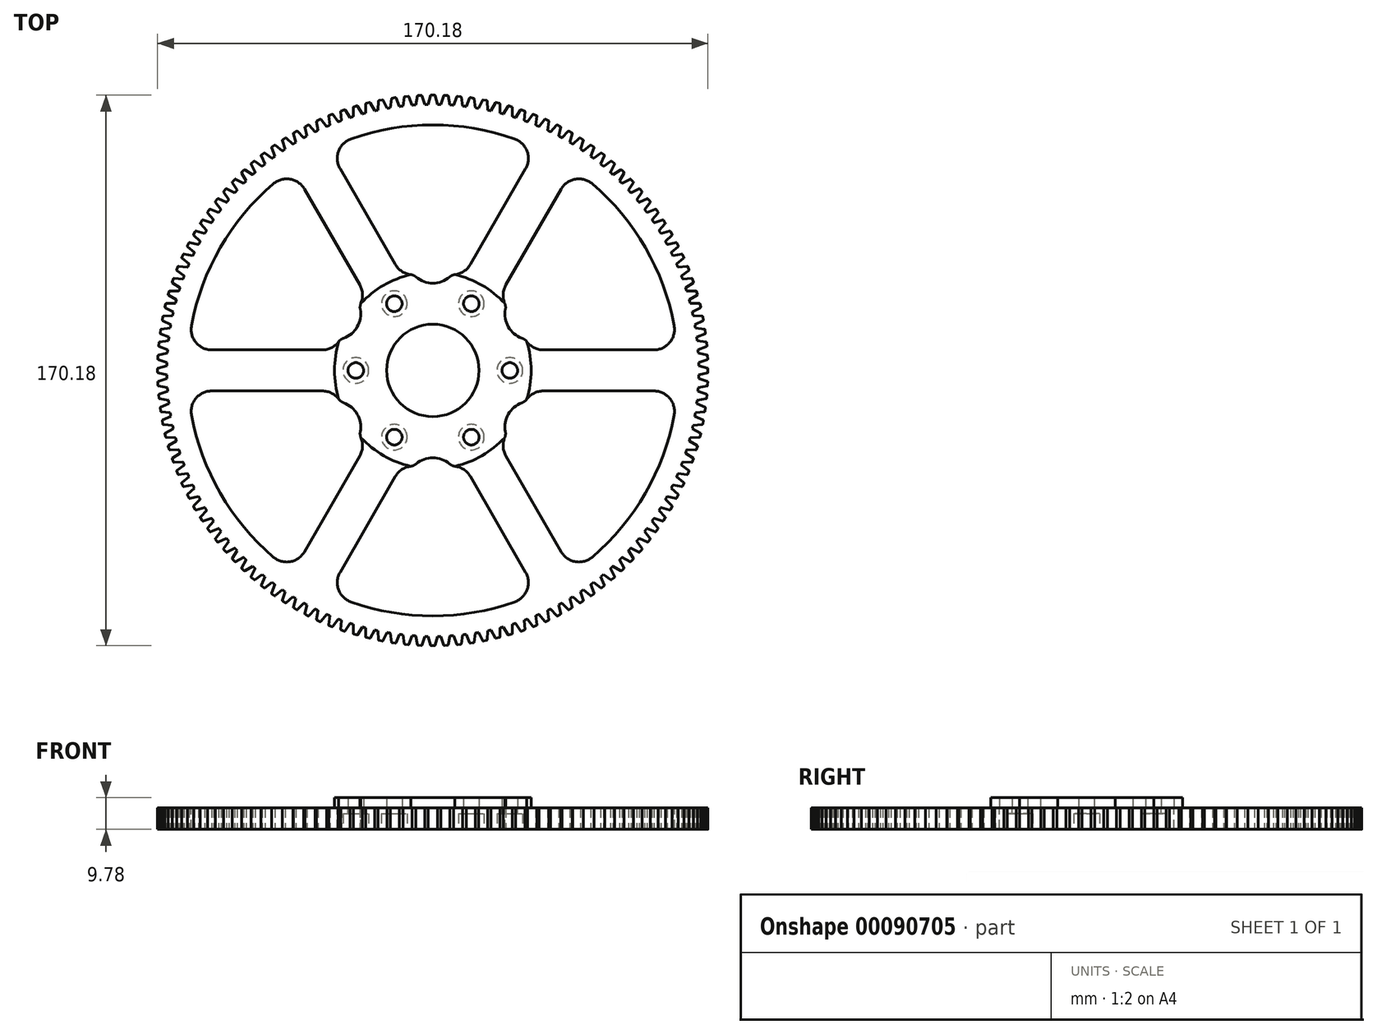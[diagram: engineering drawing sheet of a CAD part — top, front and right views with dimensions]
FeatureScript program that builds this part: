
annotation { "Feature Type Name" : "Feature", "Feature Type Description" : "" }
export const myFeature = defineFeature(function(context is Context, id is Id, definition is map)
    precondition{}
    {
        {
            var Q0;
            Q0=qCreatedBy(makeId("Top.planeOp"),FACE);
            var sketch = newSketch(context, id + "F0", { "sketchPlane" : qUnion([Q0])});
            skArc(sketch, "E0", {"start": v(-1.4, 82.23) * mm, "mid": v(-82.23, -1.4) * mm, "end": v(1.4, -82.23) * mm});
            skArc(sketch, "E1", {"start": v(1.4, -82.23) * mm, "mid": v(82.24, 0) * mm, "end": v(1.4, 82.23) * mm});
            skLineSegment(sketch, "E2", {"start": v(1.4, 82.23) * mm, "end": v(0.7, 84.97) * mm});
            skArc(sketch, "E3", {"start": v(0.7, 84.97) * mm, "mid": v(0.64, 85.06) * mm, "end": v(0.55, 85.1) * mm});
            skLineSegment(sketch, "E4", {"start": v(-1.4, 82.23) * mm, "end": v(-0.7, 84.97) * mm});
            skArc(sketch, "E5", {"start": v(-0.55, 85.1) * mm, "mid": v(-0.64, 85.06) * mm, "end": v(-0.7, 84.97) * mm});
            skLineSegment(sketch, "E6", {"start": v(-0.55, 85.1) * mm, "end": v(0.55, 85.1) * mm});
            skArc(sketch, "E7", {"start": v(1.4, 82.23) * mm, "mid": v(0, 82.24) * mm, "end": v(-1.4, 82.23) * mm});
            skSolve(sketch);
        }
        {
            var Q0;
            Q0=makeQuery(id+"F0.imprint","IMPRINT",FACE,{"disambiguationData":[TD([[makeQuery(id+"F0.imprint","IMPRINT",EDGE,{"derivedFrom":sQuery(id+"F0.wireOp",EDGE,"E0")}),1.0]])]});
            extrude(context, id + "F1", {"entities" : qUnion([Q0]), "endBound" : BoundingType.SYMMETRIC, "depth" : 6.6 * mm});
        }
        {
            var Q0;
            Q0=makeQuery(id+"F0.imprint","IMPRINT",FACE,{"disambiguationData":[TD([[makeQuery(id+"F0.imprint","IMPRINT",EDGE,{"derivedFrom":sQuery(id+"F0.wireOp",EDGE,"E2")}),1.0]])]});
            var Q1;
            Q1=makeQuery(id+"F1.opExtrude","CAP_FACE",FACE,{"disambiguationData":[OSD([sQuery(id+"F0.wireOp",EDGE,"E0"),sQuery(id+"F0.wireOp",EDGE,"E1"),sQuery(id+"F0.wireOp",EDGE,"E7")])],"isStart":false});
            var Q2;
            Q2=makeQuery(id+"F1.opExtrude","CAP_FACE",FACE,{"disambiguationData":[OSD([sQuery(id+"F0.wireOp",EDGE,"E0"),sQuery(id+"F0.wireOp",EDGE,"E1"),sQuery(id+"F0.wireOp",EDGE,"E7")])],"isStart":true});
            extrude(context, id + "F2", {"entities" : qUnion([Q0]), "endBound" : BoundingType.UP_TO_SURFACE, "endBoundEntityFace" : qUnion([Q1]), "depth" : 25.4 * mm, "hasSecondDirection" : true, "secondDirectionBound" : SecondDirectionBoundingType.UP_TO_SURFACE, "secondDirectionOppositeDirection" : true, "secondDirectionBoundEntityFace" : qUnion([Q2]), "secondDirectionDepth" : 25.4 * mm});
        }
        {
            var Q0;
            Q0=makeQuery(id+"F2.opExtrude","SWEPT_BODY",BODY,{"disambiguationData":[OSD([sQuery(id+"F0.wireOp",EDGE,"E2"),sQuery(id+"F0.wireOp",EDGE,"E3"),sQuery(id+"F0.wireOp",EDGE,"E4"),sQuery(id+"F0.wireOp",EDGE,"E5"),sQuery(id+"F0.wireOp",EDGE,"E6"),sQuery(id+"F0.wireOp",EDGE,"E7")])]});
            var Q1;
            Q1=makeQuery(id+"F1.opExtrude","CAP_EDGE",EDGE,{"disambiguationData":[OSD([sQuery(id+"F0.wireOp",EDGE,"E0"),sQuery(id+"F0.wireOp",EDGE,"E1"),sQuery(id+"F0.wireOp",EDGE,"E7")])],"isStart":false});
            circularPattern(context, id + "F3", {"operationType" : NewBodyOperationType.ADD, "entities" : qUnion([Q0]), "axis" : qUnion([Q1]), "angle" : 360 * degree, "instanceCount" : 132, "oppositeDirection" : true, "equalSpace" : true});
        }
        {
            var Q0;
            {var subQ0=sQuery(id+"F0.wireOp",EDGE,"E7");var subQ1=makeQuery(id+"F2.opExtrude","CAP_FACE",FACE,{"disambiguationData":[OSD([sQuery(id+"F0.wireOp",EDGE,"E2"),sQuery(id+"F0.wireOp",EDGE,"E3"),sQuery(id+"F0.wireOp",EDGE,"E4"),sQuery(id+"F0.wireOp",EDGE,"E5"),sQuery(id+"F0.wireOp",EDGE,"E6"),subQ0])],"isStart":false});Q0=makeQuery(id+"F3.boolean.opBoolean","MERGE",FACE,{"derivedFrom":[makeQuery(id+"F1.opExtrude","CAP_FACE",FACE,{"disambiguationData":[OSD([sQuery(id+"F0.wireOp",EDGE,"E0"),sQuery(id+"F0.wireOp",EDGE,"E1"),subQ0])],"isStart":false}),subQ1,makeQuery(id+"F3.opPattern","COPY",FACE,{"derivedFrom":subQ1,"instanceName":"1"}),makeQuery(id+"F3.opPattern","COPY",FACE,{"derivedFrom":subQ1,"instanceName":"2"}),makeQuery(id+"F3.opPattern","COPY",FACE,{"derivedFrom":subQ1,"instanceName":"3"}),makeQuery(id+"F3.opPattern","COPY",FACE,{"derivedFrom":subQ1,"instanceName":"4"}),makeQuery(id+"F3.opPattern","COPY",FACE,{"derivedFrom":subQ1,"instanceName":"5"}),makeQuery(id+"F3.opPattern","COPY",FACE,{"derivedFrom":subQ1,"instanceName":"6"}),makeQuery(id+"F3.opPattern","COPY",FACE,{"derivedFrom":subQ1,"instanceName":"7"}),makeQuery(id+"F3.opPattern","COPY",FACE,{"derivedFrom":subQ1,"instanceName":"8"}),makeQuery(id+"F3.opPattern","COPY",FACE,{"derivedFrom":subQ1,"instanceName":"9"}),makeQuery(id+"F3.opPattern","COPY",FACE,{"derivedFrom":subQ1,"instanceName":"10"}),makeQuery(id+"F3.opPattern","COPY",FACE,{"derivedFrom":subQ1,"instanceName":"11"}),makeQuery(id+"F3.opPattern","COPY",FACE,{"derivedFrom":subQ1,"instanceName":"12"}),makeQuery(id+"F3.opPattern","COPY",FACE,{"derivedFrom":subQ1,"instanceName":"13"}),makeQuery(id+"F3.opPattern","COPY",FACE,{"derivedFrom":subQ1,"instanceName":"14"}),makeQuery(id+"F3.opPattern","COPY",FACE,{"derivedFrom":subQ1,"instanceName":"15"}),makeQuery(id+"F3.opPattern","COPY",FACE,{"derivedFrom":subQ1,"instanceName":"16"}),makeQuery(id+"F3.opPattern","COPY",FACE,{"derivedFrom":subQ1,"instanceName":"17"}),makeQuery(id+"F3.opPattern","COPY",FACE,{"derivedFrom":subQ1,"instanceName":"18"}),makeQuery(id+"F3.opPattern","COPY",FACE,{"derivedFrom":subQ1,"instanceName":"19"}),makeQuery(id+"F3.opPattern","COPY",FACE,{"derivedFrom":subQ1,"instanceName":"20"}),makeQuery(id+"F3.opPattern","COPY",FACE,{"derivedFrom":subQ1,"instanceName":"21"}),makeQuery(id+"F3.opPattern","COPY",FACE,{"derivedFrom":subQ1,"instanceName":"22"}),makeQuery(id+"F3.opPattern","COPY",FACE,{"derivedFrom":subQ1,"instanceName":"23"}),makeQuery(id+"F3.opPattern","COPY",FACE,{"derivedFrom":subQ1,"instanceName":"24"}),makeQuery(id+"F3.opPattern","COPY",FACE,{"derivedFrom":subQ1,"instanceName":"25"}),makeQuery(id+"F3.opPattern","COPY",FACE,{"derivedFrom":subQ1,"instanceName":"26"}),makeQuery(id+"F3.opPattern","COPY",FACE,{"derivedFrom":subQ1,"instanceName":"27"}),makeQuery(id+"F3.opPattern","COPY",FACE,{"derivedFrom":subQ1,"instanceName":"28"}),makeQuery(id+"F3.opPattern","COPY",FACE,{"derivedFrom":subQ1,"instanceName":"29"}),makeQuery(id+"F3.opPattern","COPY",FACE,{"derivedFrom":subQ1,"instanceName":"30"}),makeQuery(id+"F3.opPattern","COPY",FACE,{"derivedFrom":subQ1,"instanceName":"31"}),makeQuery(id+"F3.opPattern","COPY",FACE,{"derivedFrom":subQ1,"instanceName":"32"}),makeQuery(id+"F3.opPattern","COPY",FACE,{"derivedFrom":subQ1,"instanceName":"33"}),makeQuery(id+"F3.opPattern","COPY",FACE,{"derivedFrom":subQ1,"instanceName":"34"}),makeQuery(id+"F3.opPattern","COPY",FACE,{"derivedFrom":subQ1,"instanceName":"35"}),makeQuery(id+"F3.opPattern","COPY",FACE,{"derivedFrom":subQ1,"instanceName":"36"}),makeQuery(id+"F3.opPattern","COPY",FACE,{"derivedFrom":subQ1,"instanceName":"37"}),makeQuery(id+"F3.opPattern","COPY",FACE,{"derivedFrom":subQ1,"instanceName":"38"}),makeQuery(id+"F3.opPattern","COPY",FACE,{"derivedFrom":subQ1,"instanceName":"39"}),makeQuery(id+"F3.opPattern","COPY",FACE,{"derivedFrom":subQ1,"instanceName":"40"}),makeQuery(id+"F3.opPattern","COPY",FACE,{"derivedFrom":subQ1,"instanceName":"41"}),makeQuery(id+"F3.opPattern","COPY",FACE,{"derivedFrom":subQ1,"instanceName":"42"}),makeQuery(id+"F3.opPattern","COPY",FACE,{"derivedFrom":subQ1,"instanceName":"43"}),makeQuery(id+"F3.opPattern","COPY",FACE,{"derivedFrom":subQ1,"instanceName":"44"}),makeQuery(id+"F3.opPattern","COPY",FACE,{"derivedFrom":subQ1,"instanceName":"45"}),makeQuery(id+"F3.opPattern","COPY",FACE,{"derivedFrom":subQ1,"instanceName":"46"}),makeQuery(id+"F3.opPattern","COPY",FACE,{"derivedFrom":subQ1,"instanceName":"47"}),makeQuery(id+"F3.opPattern","COPY",FACE,{"derivedFrom":subQ1,"instanceName":"48"}),makeQuery(id+"F3.opPattern","COPY",FACE,{"derivedFrom":subQ1,"instanceName":"49"}),makeQuery(id+"F3.opPattern","COPY",FACE,{"derivedFrom":subQ1,"instanceName":"50"}),makeQuery(id+"F3.opPattern","COPY",FACE,{"derivedFrom":subQ1,"instanceName":"51"}),makeQuery(id+"F3.opPattern","COPY",FACE,{"derivedFrom":subQ1,"instanceName":"52"}),makeQuery(id+"F3.opPattern","COPY",FACE,{"derivedFrom":subQ1,"instanceName":"53"}),makeQuery(id+"F3.opPattern","COPY",FACE,{"derivedFrom":subQ1,"instanceName":"54"}),makeQuery(id+"F3.opPattern","COPY",FACE,{"derivedFrom":subQ1,"instanceName":"55"}),makeQuery(id+"F3.opPattern","COPY",FACE,{"derivedFrom":subQ1,"instanceName":"56"}),makeQuery(id+"F3.opPattern","COPY",FACE,{"derivedFrom":subQ1,"instanceName":"57"}),makeQuery(id+"F3.opPattern","COPY",FACE,{"derivedFrom":subQ1,"instanceName":"58"}),makeQuery(id+"F3.opPattern","COPY",FACE,{"derivedFrom":subQ1,"instanceName":"59"}),makeQuery(id+"F3.opPattern","COPY",FACE,{"derivedFrom":subQ1,"instanceName":"60"}),makeQuery(id+"F3.opPattern","COPY",FACE,{"derivedFrom":subQ1,"instanceName":"61"}),makeQuery(id+"F3.opPattern","COPY",FACE,{"derivedFrom":subQ1,"instanceName":"62"}),makeQuery(id+"F3.opPattern","COPY",FACE,{"derivedFrom":subQ1,"instanceName":"63"}),makeQuery(id+"F3.opPattern","COPY",FACE,{"derivedFrom":subQ1,"instanceName":"64"}),makeQuery(id+"F3.opPattern","COPY",FACE,{"derivedFrom":subQ1,"instanceName":"65"}),makeQuery(id+"F3.opPattern","COPY",FACE,{"derivedFrom":subQ1,"instanceName":"66"}),makeQuery(id+"F3.opPattern","COPY",FACE,{"derivedFrom":subQ1,"instanceName":"67"}),makeQuery(id+"F3.opPattern","COPY",FACE,{"derivedFrom":subQ1,"instanceName":"68"}),makeQuery(id+"F3.opPattern","COPY",FACE,{"derivedFrom":subQ1,"instanceName":"69"}),makeQuery(id+"F3.opPattern","COPY",FACE,{"derivedFrom":subQ1,"instanceName":"70"}),makeQuery(id+"F3.opPattern","COPY",FACE,{"derivedFrom":subQ1,"instanceName":"71"}),makeQuery(id+"F3.opPattern","COPY",FACE,{"derivedFrom":subQ1,"instanceName":"72"}),makeQuery(id+"F3.opPattern","COPY",FACE,{"derivedFrom":subQ1,"instanceName":"73"}),makeQuery(id+"F3.opPattern","COPY",FACE,{"derivedFrom":subQ1,"instanceName":"74"}),makeQuery(id+"F3.opPattern","COPY",FACE,{"derivedFrom":subQ1,"instanceName":"75"}),makeQuery(id+"F3.opPattern","COPY",FACE,{"derivedFrom":subQ1,"instanceName":"76"}),makeQuery(id+"F3.opPattern","COPY",FACE,{"derivedFrom":subQ1,"instanceName":"77"}),makeQuery(id+"F3.opPattern","COPY",FACE,{"derivedFrom":subQ1,"instanceName":"78"}),makeQuery(id+"F3.opPattern","COPY",FACE,{"derivedFrom":subQ1,"instanceName":"79"}),makeQuery(id+"F3.opPattern","COPY",FACE,{"derivedFrom":subQ1,"instanceName":"80"}),makeQuery(id+"F3.opPattern","COPY",FACE,{"derivedFrom":subQ1,"instanceName":"81"}),makeQuery(id+"F3.opPattern","COPY",FACE,{"derivedFrom":subQ1,"instanceName":"82"}),makeQuery(id+"F3.opPattern","COPY",FACE,{"derivedFrom":subQ1,"instanceName":"83"}),makeQuery(id+"F3.opPattern","COPY",FACE,{"derivedFrom":subQ1,"instanceName":"84"}),makeQuery(id+"F3.opPattern","COPY",FACE,{"derivedFrom":subQ1,"instanceName":"85"}),makeQuery(id+"F3.opPattern","COPY",FACE,{"derivedFrom":subQ1,"instanceName":"86"}),makeQuery(id+"F3.opPattern","COPY",FACE,{"derivedFrom":subQ1,"instanceName":"87"}),makeQuery(id+"F3.opPattern","COPY",FACE,{"derivedFrom":subQ1,"instanceName":"88"}),makeQuery(id+"F3.opPattern","COPY",FACE,{"derivedFrom":subQ1,"instanceName":"89"}),makeQuery(id+"F3.opPattern","COPY",FACE,{"derivedFrom":subQ1,"instanceName":"90"}),makeQuery(id+"F3.opPattern","COPY",FACE,{"derivedFrom":subQ1,"instanceName":"91"}),makeQuery(id+"F3.opPattern","COPY",FACE,{"derivedFrom":subQ1,"instanceName":"92"}),makeQuery(id+"F3.opPattern","COPY",FACE,{"derivedFrom":subQ1,"instanceName":"93"}),makeQuery(id+"F3.opPattern","COPY",FACE,{"derivedFrom":subQ1,"instanceName":"94"}),makeQuery(id+"F3.opPattern","COPY",FACE,{"derivedFrom":subQ1,"instanceName":"95"}),makeQuery(id+"F3.opPattern","COPY",FACE,{"derivedFrom":subQ1,"instanceName":"96"}),makeQuery(id+"F3.opPattern","COPY",FACE,{"derivedFrom":subQ1,"instanceName":"97"}),makeQuery(id+"F3.opPattern","COPY",FACE,{"derivedFrom":subQ1,"instanceName":"98"}),makeQuery(id+"F3.opPattern","COPY",FACE,{"derivedFrom":subQ1,"instanceName":"99"}),makeQuery(id+"F3.opPattern","COPY",FACE,{"derivedFrom":subQ1,"instanceName":"100"}),makeQuery(id+"F3.opPattern","COPY",FACE,{"derivedFrom":subQ1,"instanceName":"101"}),makeQuery(id+"F3.opPattern","COPY",FACE,{"derivedFrom":subQ1,"instanceName":"102"}),makeQuery(id+"F3.opPattern","COPY",FACE,{"derivedFrom":subQ1,"instanceName":"103"}),makeQuery(id+"F3.opPattern","COPY",FACE,{"derivedFrom":subQ1,"instanceName":"104"}),makeQuery(id+"F3.opPattern","COPY",FACE,{"derivedFrom":subQ1,"instanceName":"105"}),makeQuery(id+"F3.opPattern","COPY",FACE,{"derivedFrom":subQ1,"instanceName":"106"}),makeQuery(id+"F3.opPattern","COPY",FACE,{"derivedFrom":subQ1,"instanceName":"107"}),makeQuery(id+"F3.opPattern","COPY",FACE,{"derivedFrom":subQ1,"instanceName":"108"}),makeQuery(id+"F3.opPattern","COPY",FACE,{"derivedFrom":subQ1,"instanceName":"109"}),makeQuery(id+"F3.opPattern","COPY",FACE,{"derivedFrom":subQ1,"instanceName":"110"}),makeQuery(id+"F3.opPattern","COPY",FACE,{"derivedFrom":subQ1,"instanceName":"111"}),makeQuery(id+"F3.opPattern","COPY",FACE,{"derivedFrom":subQ1,"instanceName":"112"}),makeQuery(id+"F3.opPattern","COPY",FACE,{"derivedFrom":subQ1,"instanceName":"113"}),makeQuery(id+"F3.opPattern","COPY",FACE,{"derivedFrom":subQ1,"instanceName":"114"}),makeQuery(id+"F3.opPattern","COPY",FACE,{"derivedFrom":subQ1,"instanceName":"115"}),makeQuery(id+"F3.opPattern","COPY",FACE,{"derivedFrom":subQ1,"instanceName":"116"}),makeQuery(id+"F3.opPattern","COPY",FACE,{"derivedFrom":subQ1,"instanceName":"117"}),makeQuery(id+"F3.opPattern","COPY",FACE,{"derivedFrom":subQ1,"instanceName":"118"}),makeQuery(id+"F3.opPattern","COPY",FACE,{"derivedFrom":subQ1,"instanceName":"119"}),makeQuery(id+"F3.opPattern","COPY",FACE,{"derivedFrom":subQ1,"instanceName":"120"}),makeQuery(id+"F3.opPattern","COPY",FACE,{"derivedFrom":subQ1,"instanceName":"121"}),makeQuery(id+"F3.opPattern","COPY",FACE,{"derivedFrom":subQ1,"instanceName":"122"}),makeQuery(id+"F3.opPattern","COPY",FACE,{"derivedFrom":subQ1,"instanceName":"123"}),makeQuery(id+"F3.opPattern","COPY",FACE,{"derivedFrom":subQ1,"instanceName":"124"}),makeQuery(id+"F3.opPattern","COPY",FACE,{"derivedFrom":subQ1,"instanceName":"125"}),makeQuery(id+"F3.opPattern","COPY",FACE,{"derivedFrom":subQ1,"instanceName":"126"}),makeQuery(id+"F3.opPattern","COPY",FACE,{"derivedFrom":subQ1,"instanceName":"127"}),makeQuery(id+"F3.opPattern","COPY",FACE,{"derivedFrom":subQ1,"instanceName":"128"}),makeQuery(id+"F3.opPattern","COPY",FACE,{"derivedFrom":subQ1,"instanceName":"129"}),makeQuery(id+"F3.opPattern","COPY",FACE,{"derivedFrom":subQ1,"instanceName":"130"}),makeQuery(id+"F3.opPattern","COPY",FACE,{"derivedFrom":subQ1,"instanceName":"131"})]});}
            var sketch = newSketch(context, id + "F4", { "sketchPlane" : qUnion([Q0])});
            skCircle(sketch, "E8", {"center": v(0, 0) * mm, "radius": 14.29 * mm});
            skCircle(sketch, "E9.cCircle", {"center": v(0, 0) * mm, "radius": 23.81 * mm, "construction": true});
            skLineSegment(sketch, "E9.0", {"start": v(23.81, 0) * mm, "end": v(11.9, -20.62) * mm, "construction": true});
            skLineSegment(sketch, "E9.1", {"start": v(11.9, -20.62) * mm, "end": v(-11.9, -20.62) * mm, "construction": true});
            skLineSegment(sketch, "E9.2", {"start": v(-11.9, -20.62) * mm, "end": v(-23.81, 0) * mm, "construction": true});
            skLineSegment(sketch, "E9.3", {"start": v(-23.81, 0) * mm, "end": v(-11.9, 20.62) * mm, "construction": true});
            skLineSegment(sketch, "E9.4", {"start": v(-11.9, 20.62) * mm, "end": v(11.9, 20.62) * mm, "construction": true});
            skLineSegment(sketch, "E9.5", {"start": v(11.9, 20.62) * mm, "end": v(23.81, 0) * mm, "construction": true});
            skCircle(sketch, "E10", {"center": v(-11.9, 20.62) * mm, "radius": 2.41 * mm});
            skCircle(sketch, "E11", {"center": v(-23.81, 0) * mm, "radius": 2.41 * mm});
            skCircle(sketch, "E12", {"center": v(-11.9, -20.62) * mm, "radius": 2.41 * mm});
            skCircle(sketch, "E13", {"center": v(11.9, -20.62) * mm, "radius": 2.41 * mm});
            skCircle(sketch, "E14", {"center": v(23.81, 0) * mm, "radius": 2.41 * mm});
            skCircle(sketch, "E15", {"center": v(11.9, 20.62) * mm, "radius": 2.41 * mm});
            skSolve(sketch);
        }
        {
            var Q0;
            Q0=qSketchRegion(id+"F4",true);
            extrude(context, id + "F5", {"entities" : qUnion([Q0]), "operationType" : NewBodyOperationType.REMOVE, "endBound" : BoundingType.THROUGH_ALL, "oppositeDirection" : true, "depth" : 25.4 * mm});
        }
        {
            var Q0;
            {var subQ0=sQuery(id+"F0.wireOp",EDGE,"E7");var subQ1=makeQuery(id+"F2.opExtrude","CAP_FACE",FACE,{"disambiguationData":[OSD([sQuery(id+"F0.wireOp",EDGE,"E2"),sQuery(id+"F0.wireOp",EDGE,"E3"),sQuery(id+"F0.wireOp",EDGE,"E4"),sQuery(id+"F0.wireOp",EDGE,"E5"),sQuery(id+"F0.wireOp",EDGE,"E6"),subQ0])],"isStart":false});Q0=makeQuery(id+"F3.boolean.opBoolean","MERGE",FACE,{"derivedFrom":[makeQuery(id+"F1.opExtrude","CAP_FACE",FACE,{"disambiguationData":[OSD([sQuery(id+"F0.wireOp",EDGE,"E0"),sQuery(id+"F0.wireOp",EDGE,"E1"),subQ0])],"isStart":false}),subQ1,makeQuery(id+"F3.opPattern","COPY",FACE,{"derivedFrom":subQ1,"instanceName":"1"}),makeQuery(id+"F3.opPattern","COPY",FACE,{"derivedFrom":subQ1,"instanceName":"2"}),makeQuery(id+"F3.opPattern","COPY",FACE,{"derivedFrom":subQ1,"instanceName":"3"}),makeQuery(id+"F3.opPattern","COPY",FACE,{"derivedFrom":subQ1,"instanceName":"4"}),makeQuery(id+"F3.opPattern","COPY",FACE,{"derivedFrom":subQ1,"instanceName":"5"}),makeQuery(id+"F3.opPattern","COPY",FACE,{"derivedFrom":subQ1,"instanceName":"6"}),makeQuery(id+"F3.opPattern","COPY",FACE,{"derivedFrom":subQ1,"instanceName":"7"}),makeQuery(id+"F3.opPattern","COPY",FACE,{"derivedFrom":subQ1,"instanceName":"8"}),makeQuery(id+"F3.opPattern","COPY",FACE,{"derivedFrom":subQ1,"instanceName":"9"}),makeQuery(id+"F3.opPattern","COPY",FACE,{"derivedFrom":subQ1,"instanceName":"10"}),makeQuery(id+"F3.opPattern","COPY",FACE,{"derivedFrom":subQ1,"instanceName":"11"}),makeQuery(id+"F3.opPattern","COPY",FACE,{"derivedFrom":subQ1,"instanceName":"12"}),makeQuery(id+"F3.opPattern","COPY",FACE,{"derivedFrom":subQ1,"instanceName":"13"}),makeQuery(id+"F3.opPattern","COPY",FACE,{"derivedFrom":subQ1,"instanceName":"14"}),makeQuery(id+"F3.opPattern","COPY",FACE,{"derivedFrom":subQ1,"instanceName":"15"}),makeQuery(id+"F3.opPattern","COPY",FACE,{"derivedFrom":subQ1,"instanceName":"16"}),makeQuery(id+"F3.opPattern","COPY",FACE,{"derivedFrom":subQ1,"instanceName":"17"}),makeQuery(id+"F3.opPattern","COPY",FACE,{"derivedFrom":subQ1,"instanceName":"18"}),makeQuery(id+"F3.opPattern","COPY",FACE,{"derivedFrom":subQ1,"instanceName":"19"}),makeQuery(id+"F3.opPattern","COPY",FACE,{"derivedFrom":subQ1,"instanceName":"20"}),makeQuery(id+"F3.opPattern","COPY",FACE,{"derivedFrom":subQ1,"instanceName":"21"}),makeQuery(id+"F3.opPattern","COPY",FACE,{"derivedFrom":subQ1,"instanceName":"22"}),makeQuery(id+"F3.opPattern","COPY",FACE,{"derivedFrom":subQ1,"instanceName":"23"}),makeQuery(id+"F3.opPattern","COPY",FACE,{"derivedFrom":subQ1,"instanceName":"24"}),makeQuery(id+"F3.opPattern","COPY",FACE,{"derivedFrom":subQ1,"instanceName":"25"}),makeQuery(id+"F3.opPattern","COPY",FACE,{"derivedFrom":subQ1,"instanceName":"26"}),makeQuery(id+"F3.opPattern","COPY",FACE,{"derivedFrom":subQ1,"instanceName":"27"}),makeQuery(id+"F3.opPattern","COPY",FACE,{"derivedFrom":subQ1,"instanceName":"28"}),makeQuery(id+"F3.opPattern","COPY",FACE,{"derivedFrom":subQ1,"instanceName":"29"}),makeQuery(id+"F3.opPattern","COPY",FACE,{"derivedFrom":subQ1,"instanceName":"30"}),makeQuery(id+"F3.opPattern","COPY",FACE,{"derivedFrom":subQ1,"instanceName":"31"}),makeQuery(id+"F3.opPattern","COPY",FACE,{"derivedFrom":subQ1,"instanceName":"32"}),makeQuery(id+"F3.opPattern","COPY",FACE,{"derivedFrom":subQ1,"instanceName":"33"}),makeQuery(id+"F3.opPattern","COPY",FACE,{"derivedFrom":subQ1,"instanceName":"34"}),makeQuery(id+"F3.opPattern","COPY",FACE,{"derivedFrom":subQ1,"instanceName":"35"}),makeQuery(id+"F3.opPattern","COPY",FACE,{"derivedFrom":subQ1,"instanceName":"36"}),makeQuery(id+"F3.opPattern","COPY",FACE,{"derivedFrom":subQ1,"instanceName":"37"}),makeQuery(id+"F3.opPattern","COPY",FACE,{"derivedFrom":subQ1,"instanceName":"38"}),makeQuery(id+"F3.opPattern","COPY",FACE,{"derivedFrom":subQ1,"instanceName":"39"}),makeQuery(id+"F3.opPattern","COPY",FACE,{"derivedFrom":subQ1,"instanceName":"40"}),makeQuery(id+"F3.opPattern","COPY",FACE,{"derivedFrom":subQ1,"instanceName":"41"}),makeQuery(id+"F3.opPattern","COPY",FACE,{"derivedFrom":subQ1,"instanceName":"42"}),makeQuery(id+"F3.opPattern","COPY",FACE,{"derivedFrom":subQ1,"instanceName":"43"}),makeQuery(id+"F3.opPattern","COPY",FACE,{"derivedFrom":subQ1,"instanceName":"44"}),makeQuery(id+"F3.opPattern","COPY",FACE,{"derivedFrom":subQ1,"instanceName":"45"}),makeQuery(id+"F3.opPattern","COPY",FACE,{"derivedFrom":subQ1,"instanceName":"46"}),makeQuery(id+"F3.opPattern","COPY",FACE,{"derivedFrom":subQ1,"instanceName":"47"}),makeQuery(id+"F3.opPattern","COPY",FACE,{"derivedFrom":subQ1,"instanceName":"48"}),makeQuery(id+"F3.opPattern","COPY",FACE,{"derivedFrom":subQ1,"instanceName":"49"}),makeQuery(id+"F3.opPattern","COPY",FACE,{"derivedFrom":subQ1,"instanceName":"50"}),makeQuery(id+"F3.opPattern","COPY",FACE,{"derivedFrom":subQ1,"instanceName":"51"}),makeQuery(id+"F3.opPattern","COPY",FACE,{"derivedFrom":subQ1,"instanceName":"52"}),makeQuery(id+"F3.opPattern","COPY",FACE,{"derivedFrom":subQ1,"instanceName":"53"}),makeQuery(id+"F3.opPattern","COPY",FACE,{"derivedFrom":subQ1,"instanceName":"54"}),makeQuery(id+"F3.opPattern","COPY",FACE,{"derivedFrom":subQ1,"instanceName":"55"}),makeQuery(id+"F3.opPattern","COPY",FACE,{"derivedFrom":subQ1,"instanceName":"56"}),makeQuery(id+"F3.opPattern","COPY",FACE,{"derivedFrom":subQ1,"instanceName":"57"}),makeQuery(id+"F3.opPattern","COPY",FACE,{"derivedFrom":subQ1,"instanceName":"58"}),makeQuery(id+"F3.opPattern","COPY",FACE,{"derivedFrom":subQ1,"instanceName":"59"}),makeQuery(id+"F3.opPattern","COPY",FACE,{"derivedFrom":subQ1,"instanceName":"60"}),makeQuery(id+"F3.opPattern","COPY",FACE,{"derivedFrom":subQ1,"instanceName":"61"}),makeQuery(id+"F3.opPattern","COPY",FACE,{"derivedFrom":subQ1,"instanceName":"62"}),makeQuery(id+"F3.opPattern","COPY",FACE,{"derivedFrom":subQ1,"instanceName":"63"}),makeQuery(id+"F3.opPattern","COPY",FACE,{"derivedFrom":subQ1,"instanceName":"64"}),makeQuery(id+"F3.opPattern","COPY",FACE,{"derivedFrom":subQ1,"instanceName":"65"}),makeQuery(id+"F3.opPattern","COPY",FACE,{"derivedFrom":subQ1,"instanceName":"66"}),makeQuery(id+"F3.opPattern","COPY",FACE,{"derivedFrom":subQ1,"instanceName":"67"}),makeQuery(id+"F3.opPattern","COPY",FACE,{"derivedFrom":subQ1,"instanceName":"68"}),makeQuery(id+"F3.opPattern","COPY",FACE,{"derivedFrom":subQ1,"instanceName":"69"}),makeQuery(id+"F3.opPattern","COPY",FACE,{"derivedFrom":subQ1,"instanceName":"70"}),makeQuery(id+"F3.opPattern","COPY",FACE,{"derivedFrom":subQ1,"instanceName":"71"}),makeQuery(id+"F3.opPattern","COPY",FACE,{"derivedFrom":subQ1,"instanceName":"72"}),makeQuery(id+"F3.opPattern","COPY",FACE,{"derivedFrom":subQ1,"instanceName":"73"}),makeQuery(id+"F3.opPattern","COPY",FACE,{"derivedFrom":subQ1,"instanceName":"74"}),makeQuery(id+"F3.opPattern","COPY",FACE,{"derivedFrom":subQ1,"instanceName":"75"}),makeQuery(id+"F3.opPattern","COPY",FACE,{"derivedFrom":subQ1,"instanceName":"76"}),makeQuery(id+"F3.opPattern","COPY",FACE,{"derivedFrom":subQ1,"instanceName":"77"}),makeQuery(id+"F3.opPattern","COPY",FACE,{"derivedFrom":subQ1,"instanceName":"78"}),makeQuery(id+"F3.opPattern","COPY",FACE,{"derivedFrom":subQ1,"instanceName":"79"}),makeQuery(id+"F3.opPattern","COPY",FACE,{"derivedFrom":subQ1,"instanceName":"80"}),makeQuery(id+"F3.opPattern","COPY",FACE,{"derivedFrom":subQ1,"instanceName":"81"}),makeQuery(id+"F3.opPattern","COPY",FACE,{"derivedFrom":subQ1,"instanceName":"82"}),makeQuery(id+"F3.opPattern","COPY",FACE,{"derivedFrom":subQ1,"instanceName":"83"}),makeQuery(id+"F3.opPattern","COPY",FACE,{"derivedFrom":subQ1,"instanceName":"84"}),makeQuery(id+"F3.opPattern","COPY",FACE,{"derivedFrom":subQ1,"instanceName":"85"}),makeQuery(id+"F3.opPattern","COPY",FACE,{"derivedFrom":subQ1,"instanceName":"86"}),makeQuery(id+"F3.opPattern","COPY",FACE,{"derivedFrom":subQ1,"instanceName":"87"}),makeQuery(id+"F3.opPattern","COPY",FACE,{"derivedFrom":subQ1,"instanceName":"88"}),makeQuery(id+"F3.opPattern","COPY",FACE,{"derivedFrom":subQ1,"instanceName":"89"}),makeQuery(id+"F3.opPattern","COPY",FACE,{"derivedFrom":subQ1,"instanceName":"90"}),makeQuery(id+"F3.opPattern","COPY",FACE,{"derivedFrom":subQ1,"instanceName":"91"}),makeQuery(id+"F3.opPattern","COPY",FACE,{"derivedFrom":subQ1,"instanceName":"92"}),makeQuery(id+"F3.opPattern","COPY",FACE,{"derivedFrom":subQ1,"instanceName":"93"}),makeQuery(id+"F3.opPattern","COPY",FACE,{"derivedFrom":subQ1,"instanceName":"94"}),makeQuery(id+"F3.opPattern","COPY",FACE,{"derivedFrom":subQ1,"instanceName":"95"}),makeQuery(id+"F3.opPattern","COPY",FACE,{"derivedFrom":subQ1,"instanceName":"96"}),makeQuery(id+"F3.opPattern","COPY",FACE,{"derivedFrom":subQ1,"instanceName":"97"}),makeQuery(id+"F3.opPattern","COPY",FACE,{"derivedFrom":subQ1,"instanceName":"98"}),makeQuery(id+"F3.opPattern","COPY",FACE,{"derivedFrom":subQ1,"instanceName":"99"}),makeQuery(id+"F3.opPattern","COPY",FACE,{"derivedFrom":subQ1,"instanceName":"100"}),makeQuery(id+"F3.opPattern","COPY",FACE,{"derivedFrom":subQ1,"instanceName":"101"}),makeQuery(id+"F3.opPattern","COPY",FACE,{"derivedFrom":subQ1,"instanceName":"102"}),makeQuery(id+"F3.opPattern","COPY",FACE,{"derivedFrom":subQ1,"instanceName":"103"}),makeQuery(id+"F3.opPattern","COPY",FACE,{"derivedFrom":subQ1,"instanceName":"104"}),makeQuery(id+"F3.opPattern","COPY",FACE,{"derivedFrom":subQ1,"instanceName":"105"}),makeQuery(id+"F3.opPattern","COPY",FACE,{"derivedFrom":subQ1,"instanceName":"106"}),makeQuery(id+"F3.opPattern","COPY",FACE,{"derivedFrom":subQ1,"instanceName":"107"}),makeQuery(id+"F3.opPattern","COPY",FACE,{"derivedFrom":subQ1,"instanceName":"108"}),makeQuery(id+"F3.opPattern","COPY",FACE,{"derivedFrom":subQ1,"instanceName":"109"}),makeQuery(id+"F3.opPattern","COPY",FACE,{"derivedFrom":subQ1,"instanceName":"110"}),makeQuery(id+"F3.opPattern","COPY",FACE,{"derivedFrom":subQ1,"instanceName":"111"}),makeQuery(id+"F3.opPattern","COPY",FACE,{"derivedFrom":subQ1,"instanceName":"112"}),makeQuery(id+"F3.opPattern","COPY",FACE,{"derivedFrom":subQ1,"instanceName":"113"}),makeQuery(id+"F3.opPattern","COPY",FACE,{"derivedFrom":subQ1,"instanceName":"114"}),makeQuery(id+"F3.opPattern","COPY",FACE,{"derivedFrom":subQ1,"instanceName":"115"}),makeQuery(id+"F3.opPattern","COPY",FACE,{"derivedFrom":subQ1,"instanceName":"116"}),makeQuery(id+"F3.opPattern","COPY",FACE,{"derivedFrom":subQ1,"instanceName":"117"}),makeQuery(id+"F3.opPattern","COPY",FACE,{"derivedFrom":subQ1,"instanceName":"118"}),makeQuery(id+"F3.opPattern","COPY",FACE,{"derivedFrom":subQ1,"instanceName":"119"}),makeQuery(id+"F3.opPattern","COPY",FACE,{"derivedFrom":subQ1,"instanceName":"120"}),makeQuery(id+"F3.opPattern","COPY",FACE,{"derivedFrom":subQ1,"instanceName":"121"}),makeQuery(id+"F3.opPattern","COPY",FACE,{"derivedFrom":subQ1,"instanceName":"122"}),makeQuery(id+"F3.opPattern","COPY",FACE,{"derivedFrom":subQ1,"instanceName":"123"}),makeQuery(id+"F3.opPattern","COPY",FACE,{"derivedFrom":subQ1,"instanceName":"124"}),makeQuery(id+"F3.opPattern","COPY",FACE,{"derivedFrom":subQ1,"instanceName":"125"}),makeQuery(id+"F3.opPattern","COPY",FACE,{"derivedFrom":subQ1,"instanceName":"126"}),makeQuery(id+"F3.opPattern","COPY",FACE,{"derivedFrom":subQ1,"instanceName":"127"}),makeQuery(id+"F3.opPattern","COPY",FACE,{"derivedFrom":subQ1,"instanceName":"128"}),makeQuery(id+"F3.opPattern","COPY",FACE,{"derivedFrom":subQ1,"instanceName":"129"}),makeQuery(id+"F3.opPattern","COPY",FACE,{"derivedFrom":subQ1,"instanceName":"130"}),makeQuery(id+"F3.opPattern","COPY",FACE,{"derivedFrom":subQ1,"instanceName":"131"})]});}
            var sketch = newSketch(context, id + "F6", { "sketchPlane" : qUnion([Q0])});
            skArc(sketch, "E16", {"start": v(-37.95, 65.73) * mm, "mid": v(-65.73, 37.95) * mm, "end": v(-75.9, 0) * mm});
            skArc(sketch, "E17", {"start": v(-15.08, 26.12) * mm, "mid": v(-26.12, 15.08) * mm, "end": v(-30.16, 0) * mm});
            skLineSegment(sketch, "E18", {"start": v(-15.08, 26.12) * mm, "end": v(-37.95, 65.73) * mm, "construction": true});
            skLineSegment(sketch, "E19", {"start": v(-30.16, 0) * mm, "end": v(-75.9, 0) * mm, "construction": true});
            skPoint(sketch, "E20", {"position": v(-23.81, 0) * mm});
            skLineSegment(sketch, "E21.0", {"start": v(-29.49, 6.35) * mm, "end": v(-75.63, 6.35) * mm});
            skLineSegment(sketch, "E22.0", {"start": v(-20.24, 22.36) * mm, "end": v(-43.31, 62.32) * mm});
            skPoint(sketch, "E23", {"position": v(-11.9, 20.62) * mm});
            skArc(sketch, "E24", {"start": v(-28.56, 9.7) * mm, "mid": v(-23.37, 13.5) * mm, "end": v(-22.69, 19.88) * mm});
            skCircle(sketch, "E25", {"center": v(0, 0) * mm, "radius": 34.93 * mm, "construction": true});
            skLineSegment(sketch, "E26", {"start": v(-26.12, 15.08) * mm, "end": v(0, 0) * mm, "construction": true});
            skSolve(sketch);
        }
        {
            var Q0;
            {var subQ0=sQuery(id+"F6.wireOp",EDGE,"E21.0");Q0=makeQuery(id+"F6.imprint","IMPRINT",FACE,{"disambiguationData":[TD([[makeQuery(id+"F6.imprint","IMPRINT",EDGE,{"derivedFrom":subQ0}),-1.0]])]});}
            var Q1;
            {var subQ0=sQuery(id+"F6.wireOp",EDGE,"E24");Q1=makeQuery(id+"F6.imprint","IMPRINT",FACE,{"disambiguationData":[TD([[makeQuery(id+"F6.imprint","IMPRINT",EDGE,{"derivedFrom":subQ0}),1.0]])]});}
            var Q2;
            {var subQ0=sQuery(id+"F0.wireOp",EDGE,"E7");var subQ1=makeQuery(id+"F2.opExtrude","CAP_FACE",FACE,{"disambiguationData":[OSD([sQuery(id+"F0.wireOp",EDGE,"E2"),sQuery(id+"F0.wireOp",EDGE,"E3"),sQuery(id+"F0.wireOp",EDGE,"E4"),sQuery(id+"F0.wireOp",EDGE,"E5"),sQuery(id+"F0.wireOp",EDGE,"E6"),subQ0])],"isStart":true});Q2=makeQuery(id+"F3.boolean.opBoolean","MERGE",FACE,{"derivedFrom":[makeQuery(id+"F1.opExtrude","CAP_FACE",FACE,{"disambiguationData":[OSD([sQuery(id+"F0.wireOp",EDGE,"E0"),sQuery(id+"F0.wireOp",EDGE,"E1"),subQ0])],"isStart":true}),subQ1,makeQuery(id+"F3.opPattern","COPY",FACE,{"derivedFrom":subQ1,"instanceName":"1"}),makeQuery(id+"F3.opPattern","COPY",FACE,{"derivedFrom":subQ1,"instanceName":"2"}),makeQuery(id+"F3.opPattern","COPY",FACE,{"derivedFrom":subQ1,"instanceName":"3"}),makeQuery(id+"F3.opPattern","COPY",FACE,{"derivedFrom":subQ1,"instanceName":"4"}),makeQuery(id+"F3.opPattern","COPY",FACE,{"derivedFrom":subQ1,"instanceName":"5"}),makeQuery(id+"F3.opPattern","COPY",FACE,{"derivedFrom":subQ1,"instanceName":"6"}),makeQuery(id+"F3.opPattern","COPY",FACE,{"derivedFrom":subQ1,"instanceName":"7"}),makeQuery(id+"F3.opPattern","COPY",FACE,{"derivedFrom":subQ1,"instanceName":"8"}),makeQuery(id+"F3.opPattern","COPY",FACE,{"derivedFrom":subQ1,"instanceName":"9"}),makeQuery(id+"F3.opPattern","COPY",FACE,{"derivedFrom":subQ1,"instanceName":"10"}),makeQuery(id+"F3.opPattern","COPY",FACE,{"derivedFrom":subQ1,"instanceName":"11"}),makeQuery(id+"F3.opPattern","COPY",FACE,{"derivedFrom":subQ1,"instanceName":"12"}),makeQuery(id+"F3.opPattern","COPY",FACE,{"derivedFrom":subQ1,"instanceName":"13"}),makeQuery(id+"F3.opPattern","COPY",FACE,{"derivedFrom":subQ1,"instanceName":"14"}),makeQuery(id+"F3.opPattern","COPY",FACE,{"derivedFrom":subQ1,"instanceName":"15"}),makeQuery(id+"F3.opPattern","COPY",FACE,{"derivedFrom":subQ1,"instanceName":"16"}),makeQuery(id+"F3.opPattern","COPY",FACE,{"derivedFrom":subQ1,"instanceName":"17"}),makeQuery(id+"F3.opPattern","COPY",FACE,{"derivedFrom":subQ1,"instanceName":"18"}),makeQuery(id+"F3.opPattern","COPY",FACE,{"derivedFrom":subQ1,"instanceName":"19"}),makeQuery(id+"F3.opPattern","COPY",FACE,{"derivedFrom":subQ1,"instanceName":"20"}),makeQuery(id+"F3.opPattern","COPY",FACE,{"derivedFrom":subQ1,"instanceName":"21"}),makeQuery(id+"F3.opPattern","COPY",FACE,{"derivedFrom":subQ1,"instanceName":"22"}),makeQuery(id+"F3.opPattern","COPY",FACE,{"derivedFrom":subQ1,"instanceName":"23"}),makeQuery(id+"F3.opPattern","COPY",FACE,{"derivedFrom":subQ1,"instanceName":"24"}),makeQuery(id+"F3.opPattern","COPY",FACE,{"derivedFrom":subQ1,"instanceName":"25"}),makeQuery(id+"F3.opPattern","COPY",FACE,{"derivedFrom":subQ1,"instanceName":"26"}),makeQuery(id+"F3.opPattern","COPY",FACE,{"derivedFrom":subQ1,"instanceName":"27"}),makeQuery(id+"F3.opPattern","COPY",FACE,{"derivedFrom":subQ1,"instanceName":"28"}),makeQuery(id+"F3.opPattern","COPY",FACE,{"derivedFrom":subQ1,"instanceName":"29"}),makeQuery(id+"F3.opPattern","COPY",FACE,{"derivedFrom":subQ1,"instanceName":"30"}),makeQuery(id+"F3.opPattern","COPY",FACE,{"derivedFrom":subQ1,"instanceName":"31"}),makeQuery(id+"F3.opPattern","COPY",FACE,{"derivedFrom":subQ1,"instanceName":"32"}),makeQuery(id+"F3.opPattern","COPY",FACE,{"derivedFrom":subQ1,"instanceName":"33"}),makeQuery(id+"F3.opPattern","COPY",FACE,{"derivedFrom":subQ1,"instanceName":"34"}),makeQuery(id+"F3.opPattern","COPY",FACE,{"derivedFrom":subQ1,"instanceName":"35"}),makeQuery(id+"F3.opPattern","COPY",FACE,{"derivedFrom":subQ1,"instanceName":"36"}),makeQuery(id+"F3.opPattern","COPY",FACE,{"derivedFrom":subQ1,"instanceName":"37"}),makeQuery(id+"F3.opPattern","COPY",FACE,{"derivedFrom":subQ1,"instanceName":"38"}),makeQuery(id+"F3.opPattern","COPY",FACE,{"derivedFrom":subQ1,"instanceName":"39"}),makeQuery(id+"F3.opPattern","COPY",FACE,{"derivedFrom":subQ1,"instanceName":"40"}),makeQuery(id+"F3.opPattern","COPY",FACE,{"derivedFrom":subQ1,"instanceName":"41"}),makeQuery(id+"F3.opPattern","COPY",FACE,{"derivedFrom":subQ1,"instanceName":"42"}),makeQuery(id+"F3.opPattern","COPY",FACE,{"derivedFrom":subQ1,"instanceName":"43"}),makeQuery(id+"F3.opPattern","COPY",FACE,{"derivedFrom":subQ1,"instanceName":"44"}),makeQuery(id+"F3.opPattern","COPY",FACE,{"derivedFrom":subQ1,"instanceName":"45"}),makeQuery(id+"F3.opPattern","COPY",FACE,{"derivedFrom":subQ1,"instanceName":"46"}),makeQuery(id+"F3.opPattern","COPY",FACE,{"derivedFrom":subQ1,"instanceName":"47"}),makeQuery(id+"F3.opPattern","COPY",FACE,{"derivedFrom":subQ1,"instanceName":"48"}),makeQuery(id+"F3.opPattern","COPY",FACE,{"derivedFrom":subQ1,"instanceName":"49"}),makeQuery(id+"F3.opPattern","COPY",FACE,{"derivedFrom":subQ1,"instanceName":"50"}),makeQuery(id+"F3.opPattern","COPY",FACE,{"derivedFrom":subQ1,"instanceName":"51"}),makeQuery(id+"F3.opPattern","COPY",FACE,{"derivedFrom":subQ1,"instanceName":"52"}),makeQuery(id+"F3.opPattern","COPY",FACE,{"derivedFrom":subQ1,"instanceName":"53"}),makeQuery(id+"F3.opPattern","COPY",FACE,{"derivedFrom":subQ1,"instanceName":"54"}),makeQuery(id+"F3.opPattern","COPY",FACE,{"derivedFrom":subQ1,"instanceName":"55"}),makeQuery(id+"F3.opPattern","COPY",FACE,{"derivedFrom":subQ1,"instanceName":"56"}),makeQuery(id+"F3.opPattern","COPY",FACE,{"derivedFrom":subQ1,"instanceName":"57"}),makeQuery(id+"F3.opPattern","COPY",FACE,{"derivedFrom":subQ1,"instanceName":"58"}),makeQuery(id+"F3.opPattern","COPY",FACE,{"derivedFrom":subQ1,"instanceName":"59"}),makeQuery(id+"F3.opPattern","COPY",FACE,{"derivedFrom":subQ1,"instanceName":"60"}),makeQuery(id+"F3.opPattern","COPY",FACE,{"derivedFrom":subQ1,"instanceName":"61"}),makeQuery(id+"F3.opPattern","COPY",FACE,{"derivedFrom":subQ1,"instanceName":"62"}),makeQuery(id+"F3.opPattern","COPY",FACE,{"derivedFrom":subQ1,"instanceName":"63"}),makeQuery(id+"F3.opPattern","COPY",FACE,{"derivedFrom":subQ1,"instanceName":"64"}),makeQuery(id+"F3.opPattern","COPY",FACE,{"derivedFrom":subQ1,"instanceName":"65"}),makeQuery(id+"F3.opPattern","COPY",FACE,{"derivedFrom":subQ1,"instanceName":"66"}),makeQuery(id+"F3.opPattern","COPY",FACE,{"derivedFrom":subQ1,"instanceName":"67"}),makeQuery(id+"F3.opPattern","COPY",FACE,{"derivedFrom":subQ1,"instanceName":"68"}),makeQuery(id+"F3.opPattern","COPY",FACE,{"derivedFrom":subQ1,"instanceName":"69"}),makeQuery(id+"F3.opPattern","COPY",FACE,{"derivedFrom":subQ1,"instanceName":"70"}),makeQuery(id+"F3.opPattern","COPY",FACE,{"derivedFrom":subQ1,"instanceName":"71"}),makeQuery(id+"F3.opPattern","COPY",FACE,{"derivedFrom":subQ1,"instanceName":"72"}),makeQuery(id+"F3.opPattern","COPY",FACE,{"derivedFrom":subQ1,"instanceName":"73"}),makeQuery(id+"F3.opPattern","COPY",FACE,{"derivedFrom":subQ1,"instanceName":"74"}),makeQuery(id+"F3.opPattern","COPY",FACE,{"derivedFrom":subQ1,"instanceName":"75"}),makeQuery(id+"F3.opPattern","COPY",FACE,{"derivedFrom":subQ1,"instanceName":"76"}),makeQuery(id+"F3.opPattern","COPY",FACE,{"derivedFrom":subQ1,"instanceName":"77"}),makeQuery(id+"F3.opPattern","COPY",FACE,{"derivedFrom":subQ1,"instanceName":"78"}),makeQuery(id+"F3.opPattern","COPY",FACE,{"derivedFrom":subQ1,"instanceName":"79"}),makeQuery(id+"F3.opPattern","COPY",FACE,{"derivedFrom":subQ1,"instanceName":"80"}),makeQuery(id+"F3.opPattern","COPY",FACE,{"derivedFrom":subQ1,"instanceName":"81"}),makeQuery(id+"F3.opPattern","COPY",FACE,{"derivedFrom":subQ1,"instanceName":"82"}),makeQuery(id+"F3.opPattern","COPY",FACE,{"derivedFrom":subQ1,"instanceName":"83"}),makeQuery(id+"F3.opPattern","COPY",FACE,{"derivedFrom":subQ1,"instanceName":"84"}),makeQuery(id+"F3.opPattern","COPY",FACE,{"derivedFrom":subQ1,"instanceName":"85"}),makeQuery(id+"F3.opPattern","COPY",FACE,{"derivedFrom":subQ1,"instanceName":"86"}),makeQuery(id+"F3.opPattern","COPY",FACE,{"derivedFrom":subQ1,"instanceName":"87"}),makeQuery(id+"F3.opPattern","COPY",FACE,{"derivedFrom":subQ1,"instanceName":"88"}),makeQuery(id+"F3.opPattern","COPY",FACE,{"derivedFrom":subQ1,"instanceName":"89"}),makeQuery(id+"F3.opPattern","COPY",FACE,{"derivedFrom":subQ1,"instanceName":"90"}),makeQuery(id+"F3.opPattern","COPY",FACE,{"derivedFrom":subQ1,"instanceName":"91"}),makeQuery(id+"F3.opPattern","COPY",FACE,{"derivedFrom":subQ1,"instanceName":"92"}),makeQuery(id+"F3.opPattern","COPY",FACE,{"derivedFrom":subQ1,"instanceName":"93"}),makeQuery(id+"F3.opPattern","COPY",FACE,{"derivedFrom":subQ1,"instanceName":"94"}),makeQuery(id+"F3.opPattern","COPY",FACE,{"derivedFrom":subQ1,"instanceName":"95"}),makeQuery(id+"F3.opPattern","COPY",FACE,{"derivedFrom":subQ1,"instanceName":"96"}),makeQuery(id+"F3.opPattern","COPY",FACE,{"derivedFrom":subQ1,"instanceName":"97"}),makeQuery(id+"F3.opPattern","COPY",FACE,{"derivedFrom":subQ1,"instanceName":"98"}),makeQuery(id+"F3.opPattern","COPY",FACE,{"derivedFrom":subQ1,"instanceName":"99"}),makeQuery(id+"F3.opPattern","COPY",FACE,{"derivedFrom":subQ1,"instanceName":"100"}),makeQuery(id+"F3.opPattern","COPY",FACE,{"derivedFrom":subQ1,"instanceName":"101"}),makeQuery(id+"F3.opPattern","COPY",FACE,{"derivedFrom":subQ1,"instanceName":"102"}),makeQuery(id+"F3.opPattern","COPY",FACE,{"derivedFrom":subQ1,"instanceName":"103"}),makeQuery(id+"F3.opPattern","COPY",FACE,{"derivedFrom":subQ1,"instanceName":"104"}),makeQuery(id+"F3.opPattern","COPY",FACE,{"derivedFrom":subQ1,"instanceName":"105"}),makeQuery(id+"F3.opPattern","COPY",FACE,{"derivedFrom":subQ1,"instanceName":"106"}),makeQuery(id+"F3.opPattern","COPY",FACE,{"derivedFrom":subQ1,"instanceName":"107"}),makeQuery(id+"F3.opPattern","COPY",FACE,{"derivedFrom":subQ1,"instanceName":"108"}),makeQuery(id+"F3.opPattern","COPY",FACE,{"derivedFrom":subQ1,"instanceName":"109"}),makeQuery(id+"F3.opPattern","COPY",FACE,{"derivedFrom":subQ1,"instanceName":"110"}),makeQuery(id+"F3.opPattern","COPY",FACE,{"derivedFrom":subQ1,"instanceName":"111"}),makeQuery(id+"F3.opPattern","COPY",FACE,{"derivedFrom":subQ1,"instanceName":"112"}),makeQuery(id+"F3.opPattern","COPY",FACE,{"derivedFrom":subQ1,"instanceName":"113"}),makeQuery(id+"F3.opPattern","COPY",FACE,{"derivedFrom":subQ1,"instanceName":"114"}),makeQuery(id+"F3.opPattern","COPY",FACE,{"derivedFrom":subQ1,"instanceName":"115"}),makeQuery(id+"F3.opPattern","COPY",FACE,{"derivedFrom":subQ1,"instanceName":"116"}),makeQuery(id+"F3.opPattern","COPY",FACE,{"derivedFrom":subQ1,"instanceName":"117"}),makeQuery(id+"F3.opPattern","COPY",FACE,{"derivedFrom":subQ1,"instanceName":"118"}),makeQuery(id+"F3.opPattern","COPY",FACE,{"derivedFrom":subQ1,"instanceName":"119"}),makeQuery(id+"F3.opPattern","COPY",FACE,{"derivedFrom":subQ1,"instanceName":"120"}),makeQuery(id+"F3.opPattern","COPY",FACE,{"derivedFrom":subQ1,"instanceName":"121"}),makeQuery(id+"F3.opPattern","COPY",FACE,{"derivedFrom":subQ1,"instanceName":"122"}),makeQuery(id+"F3.opPattern","COPY",FACE,{"derivedFrom":subQ1,"instanceName":"123"}),makeQuery(id+"F3.opPattern","COPY",FACE,{"derivedFrom":subQ1,"instanceName":"124"}),makeQuery(id+"F3.opPattern","COPY",FACE,{"derivedFrom":subQ1,"instanceName":"125"}),makeQuery(id+"F3.opPattern","COPY",FACE,{"derivedFrom":subQ1,"instanceName":"126"}),makeQuery(id+"F3.opPattern","COPY",FACE,{"derivedFrom":subQ1,"instanceName":"127"}),makeQuery(id+"F3.opPattern","COPY",FACE,{"derivedFrom":subQ1,"instanceName":"128"}),makeQuery(id+"F3.opPattern","COPY",FACE,{"derivedFrom":subQ1,"instanceName":"129"}),makeQuery(id+"F3.opPattern","COPY",FACE,{"derivedFrom":subQ1,"instanceName":"130"}),makeQuery(id+"F3.opPattern","COPY",FACE,{"derivedFrom":subQ1,"instanceName":"131"})]});}
            extrude(context, id + "F7", {"entities" : qUnion([Q0, Q1]), "endBound" : BoundingType.UP_TO_SURFACE, "oppositeDirection" : true, "endBoundEntityFace" : qUnion([Q2]), "depth" : 25.4 * mm});
        }
        {
            var Q0;
            Q0=makeQuery(id+"F7.opExtrude","SWEPT_EDGE",EDGE,{"disambiguationData":[OSD([sQuery(id+"F6.wireOp",EDGE,"E16"),sQuery(id+"F6.wireOp",EDGE,"E21.0")])]});
            var Q1;
            Q1=makeQuery(id+"F7.opExtrude","SWEPT_EDGE",EDGE,{"disambiguationData":[OSD([sQuery(id+"F6.wireOp",EDGE,"E17"),sQuery(id+"F6.wireOp",EDGE,"E21.0")])]});
            var Q2;
            Q2=makeQuery(id+"F7.opExtrude","SWEPT_EDGE",EDGE,{"disambiguationData":[OSD([sQuery(id+"F6.wireOp",EDGE,"E17"),sQuery(id+"F6.wireOp",EDGE,"E22.0")])]});
            var Q3;
            Q3=makeQuery(id+"F7.opExtrude","SWEPT_EDGE",EDGE,{"disambiguationData":[OSD([sQuery(id+"F6.wireOp",EDGE,"E16"),sQuery(id+"F6.wireOp",EDGE,"E22.0")])]});
            fillet(context, id + "F8", {"entities" : qUnion([Q0, Q1, Q2, Q3]), "radius" : 6.35 * mm, "tangentPropagation" : true, "allowEdgeOverflow" : false});
        }
        {
            var Q0;
            Q0=makeQuery(id+"F8.opFillet","BLEND_EDGE",EDGE,{"blendedFrom":[makeQuery(id+"F7.opExtrude","SWEPT_EDGE",EDGE,{"disambiguationData":[OSD([sQuery(id+"F6.wireOp",EDGE,"E17"),sQuery(id+"F6.wireOp",EDGE,"E22.0")])]}),makeQuery(id+"F7.opExtrude","SWEPT_FACE",FACE,{"disambiguationData":[OSD([sQuery(id+"F6.wireOp",EDGE,"E24")])]})],"blendedInto":[makeQuery(id+"F7.opExtrude","SWEPT_FACE",FACE,{"disambiguationData":[OSD([sQuery(id+"F6.wireOp",EDGE,"E24")])]})]});
            var Q1;
            Q1=makeQuery(id+"F8.opFillet","BLEND_EDGE",EDGE,{"blendedFrom":[makeQuery(id+"F7.opExtrude","SWEPT_EDGE",EDGE,{"disambiguationData":[OSD([sQuery(id+"F6.wireOp",EDGE,"E17"),sQuery(id+"F6.wireOp",EDGE,"E21.0")])]}),makeQuery(id+"F7.opExtrude","SWEPT_FACE",FACE,{"disambiguationData":[OSD([sQuery(id+"F6.wireOp",EDGE,"E24")])]})],"blendedInto":[makeQuery(id+"F7.opExtrude","SWEPT_FACE",FACE,{"disambiguationData":[OSD([sQuery(id+"F6.wireOp",EDGE,"E24")])]})]});
            fillet(context, id + "F9", {"entities" : qUnion([Q0, Q1]), "radius" : 3.17 * mm, "tangentPropagation" : true, "allowEdgeOverflow" : false});
        }
        {
            var Q0;
            Q0=makeQuery(id+"F7.opExtrude","SWEPT_BODY",BODY,{"disambiguationData":[OSD([sQuery(id+"F6.wireOp",EDGE,"E16"),sQuery(id+"F6.wireOp",EDGE,"E17"),sQuery(id+"F6.wireOp",EDGE,"E21.0"),sQuery(id+"F6.wireOp",EDGE,"E22.0")])]});
            var Q1;
            Q1=makeQuery(id+"F5.boolean.opBoolean","COPY",FACE,{"derivedFrom":makeQuery(id+"F5.opExtrude","SWEPT_FACE",FACE,{"disambiguationData":[OSD([sQuery(id+"F4.wireOp",EDGE,"E8")])]})});
            circularPattern(context, id + "F10", {"operationType" : NewBodyOperationType.REMOVE, "entities" : qUnion([Q0]), "axis" : qUnion([Q1]), "angle" : 360 * degree, "instanceCount" : 6, "equalSpace" : true});
        }
        {
            var Q0;
            {var subQ0=sQuery(id+"F0.wireOp",EDGE,"E7");var subQ1=makeQuery(id+"F2.opExtrude","CAP_FACE",FACE,{"disambiguationData":[OSD([sQuery(id+"F0.wireOp",EDGE,"E2"),sQuery(id+"F0.wireOp",EDGE,"E3"),sQuery(id+"F0.wireOp",EDGE,"E4"),sQuery(id+"F0.wireOp",EDGE,"E5"),sQuery(id+"F0.wireOp",EDGE,"E6"),subQ0])],"isStart":false});Q0=makeQuery(id+"F3.boolean.opBoolean","MERGE",FACE,{"derivedFrom":[makeQuery(id+"F1.opExtrude","CAP_FACE",FACE,{"disambiguationData":[OSD([sQuery(id+"F0.wireOp",EDGE,"E0"),sQuery(id+"F0.wireOp",EDGE,"E1"),subQ0])],"isStart":false}),subQ1,makeQuery(id+"F3.opPattern","COPY",FACE,{"derivedFrom":subQ1,"instanceName":"1"}),makeQuery(id+"F3.opPattern","COPY",FACE,{"derivedFrom":subQ1,"instanceName":"2"}),makeQuery(id+"F3.opPattern","COPY",FACE,{"derivedFrom":subQ1,"instanceName":"3"}),makeQuery(id+"F3.opPattern","COPY",FACE,{"derivedFrom":subQ1,"instanceName":"4"}),makeQuery(id+"F3.opPattern","COPY",FACE,{"derivedFrom":subQ1,"instanceName":"5"}),makeQuery(id+"F3.opPattern","COPY",FACE,{"derivedFrom":subQ1,"instanceName":"6"}),makeQuery(id+"F3.opPattern","COPY",FACE,{"derivedFrom":subQ1,"instanceName":"7"}),makeQuery(id+"F3.opPattern","COPY",FACE,{"derivedFrom":subQ1,"instanceName":"8"}),makeQuery(id+"F3.opPattern","COPY",FACE,{"derivedFrom":subQ1,"instanceName":"9"}),makeQuery(id+"F3.opPattern","COPY",FACE,{"derivedFrom":subQ1,"instanceName":"10"}),makeQuery(id+"F3.opPattern","COPY",FACE,{"derivedFrom":subQ1,"instanceName":"11"}),makeQuery(id+"F3.opPattern","COPY",FACE,{"derivedFrom":subQ1,"instanceName":"12"}),makeQuery(id+"F3.opPattern","COPY",FACE,{"derivedFrom":subQ1,"instanceName":"13"}),makeQuery(id+"F3.opPattern","COPY",FACE,{"derivedFrom":subQ1,"instanceName":"14"}),makeQuery(id+"F3.opPattern","COPY",FACE,{"derivedFrom":subQ1,"instanceName":"15"}),makeQuery(id+"F3.opPattern","COPY",FACE,{"derivedFrom":subQ1,"instanceName":"16"}),makeQuery(id+"F3.opPattern","COPY",FACE,{"derivedFrom":subQ1,"instanceName":"17"}),makeQuery(id+"F3.opPattern","COPY",FACE,{"derivedFrom":subQ1,"instanceName":"18"}),makeQuery(id+"F3.opPattern","COPY",FACE,{"derivedFrom":subQ1,"instanceName":"19"}),makeQuery(id+"F3.opPattern","COPY",FACE,{"derivedFrom":subQ1,"instanceName":"20"}),makeQuery(id+"F3.opPattern","COPY",FACE,{"derivedFrom":subQ1,"instanceName":"21"}),makeQuery(id+"F3.opPattern","COPY",FACE,{"derivedFrom":subQ1,"instanceName":"22"}),makeQuery(id+"F3.opPattern","COPY",FACE,{"derivedFrom":subQ1,"instanceName":"23"}),makeQuery(id+"F3.opPattern","COPY",FACE,{"derivedFrom":subQ1,"instanceName":"24"}),makeQuery(id+"F3.opPattern","COPY",FACE,{"derivedFrom":subQ1,"instanceName":"25"}),makeQuery(id+"F3.opPattern","COPY",FACE,{"derivedFrom":subQ1,"instanceName":"26"}),makeQuery(id+"F3.opPattern","COPY",FACE,{"derivedFrom":subQ1,"instanceName":"27"}),makeQuery(id+"F3.opPattern","COPY",FACE,{"derivedFrom":subQ1,"instanceName":"28"}),makeQuery(id+"F3.opPattern","COPY",FACE,{"derivedFrom":subQ1,"instanceName":"29"}),makeQuery(id+"F3.opPattern","COPY",FACE,{"derivedFrom":subQ1,"instanceName":"30"}),makeQuery(id+"F3.opPattern","COPY",FACE,{"derivedFrom":subQ1,"instanceName":"31"}),makeQuery(id+"F3.opPattern","COPY",FACE,{"derivedFrom":subQ1,"instanceName":"32"}),makeQuery(id+"F3.opPattern","COPY",FACE,{"derivedFrom":subQ1,"instanceName":"33"}),makeQuery(id+"F3.opPattern","COPY",FACE,{"derivedFrom":subQ1,"instanceName":"34"}),makeQuery(id+"F3.opPattern","COPY",FACE,{"derivedFrom":subQ1,"instanceName":"35"}),makeQuery(id+"F3.opPattern","COPY",FACE,{"derivedFrom":subQ1,"instanceName":"36"}),makeQuery(id+"F3.opPattern","COPY",FACE,{"derivedFrom":subQ1,"instanceName":"37"}),makeQuery(id+"F3.opPattern","COPY",FACE,{"derivedFrom":subQ1,"instanceName":"38"}),makeQuery(id+"F3.opPattern","COPY",FACE,{"derivedFrom":subQ1,"instanceName":"39"}),makeQuery(id+"F3.opPattern","COPY",FACE,{"derivedFrom":subQ1,"instanceName":"40"}),makeQuery(id+"F3.opPattern","COPY",FACE,{"derivedFrom":subQ1,"instanceName":"41"}),makeQuery(id+"F3.opPattern","COPY",FACE,{"derivedFrom":subQ1,"instanceName":"42"}),makeQuery(id+"F3.opPattern","COPY",FACE,{"derivedFrom":subQ1,"instanceName":"43"}),makeQuery(id+"F3.opPattern","COPY",FACE,{"derivedFrom":subQ1,"instanceName":"44"}),makeQuery(id+"F3.opPattern","COPY",FACE,{"derivedFrom":subQ1,"instanceName":"45"}),makeQuery(id+"F3.opPattern","COPY",FACE,{"derivedFrom":subQ1,"instanceName":"46"}),makeQuery(id+"F3.opPattern","COPY",FACE,{"derivedFrom":subQ1,"instanceName":"47"}),makeQuery(id+"F3.opPattern","COPY",FACE,{"derivedFrom":subQ1,"instanceName":"48"}),makeQuery(id+"F3.opPattern","COPY",FACE,{"derivedFrom":subQ1,"instanceName":"49"}),makeQuery(id+"F3.opPattern","COPY",FACE,{"derivedFrom":subQ1,"instanceName":"50"}),makeQuery(id+"F3.opPattern","COPY",FACE,{"derivedFrom":subQ1,"instanceName":"51"}),makeQuery(id+"F3.opPattern","COPY",FACE,{"derivedFrom":subQ1,"instanceName":"52"}),makeQuery(id+"F3.opPattern","COPY",FACE,{"derivedFrom":subQ1,"instanceName":"53"}),makeQuery(id+"F3.opPattern","COPY",FACE,{"derivedFrom":subQ1,"instanceName":"54"}),makeQuery(id+"F3.opPattern","COPY",FACE,{"derivedFrom":subQ1,"instanceName":"55"}),makeQuery(id+"F3.opPattern","COPY",FACE,{"derivedFrom":subQ1,"instanceName":"56"}),makeQuery(id+"F3.opPattern","COPY",FACE,{"derivedFrom":subQ1,"instanceName":"57"}),makeQuery(id+"F3.opPattern","COPY",FACE,{"derivedFrom":subQ1,"instanceName":"58"}),makeQuery(id+"F3.opPattern","COPY",FACE,{"derivedFrom":subQ1,"instanceName":"59"}),makeQuery(id+"F3.opPattern","COPY",FACE,{"derivedFrom":subQ1,"instanceName":"60"}),makeQuery(id+"F3.opPattern","COPY",FACE,{"derivedFrom":subQ1,"instanceName":"61"}),makeQuery(id+"F3.opPattern","COPY",FACE,{"derivedFrom":subQ1,"instanceName":"62"}),makeQuery(id+"F3.opPattern","COPY",FACE,{"derivedFrom":subQ1,"instanceName":"63"}),makeQuery(id+"F3.opPattern","COPY",FACE,{"derivedFrom":subQ1,"instanceName":"64"}),makeQuery(id+"F3.opPattern","COPY",FACE,{"derivedFrom":subQ1,"instanceName":"65"}),makeQuery(id+"F3.opPattern","COPY",FACE,{"derivedFrom":subQ1,"instanceName":"66"}),makeQuery(id+"F3.opPattern","COPY",FACE,{"derivedFrom":subQ1,"instanceName":"67"}),makeQuery(id+"F3.opPattern","COPY",FACE,{"derivedFrom":subQ1,"instanceName":"68"}),makeQuery(id+"F3.opPattern","COPY",FACE,{"derivedFrom":subQ1,"instanceName":"69"}),makeQuery(id+"F3.opPattern","COPY",FACE,{"derivedFrom":subQ1,"instanceName":"70"}),makeQuery(id+"F3.opPattern","COPY",FACE,{"derivedFrom":subQ1,"instanceName":"71"}),makeQuery(id+"F3.opPattern","COPY",FACE,{"derivedFrom":subQ1,"instanceName":"72"}),makeQuery(id+"F3.opPattern","COPY",FACE,{"derivedFrom":subQ1,"instanceName":"73"}),makeQuery(id+"F3.opPattern","COPY",FACE,{"derivedFrom":subQ1,"instanceName":"74"}),makeQuery(id+"F3.opPattern","COPY",FACE,{"derivedFrom":subQ1,"instanceName":"75"}),makeQuery(id+"F3.opPattern","COPY",FACE,{"derivedFrom":subQ1,"instanceName":"76"}),makeQuery(id+"F3.opPattern","COPY",FACE,{"derivedFrom":subQ1,"instanceName":"77"}),makeQuery(id+"F3.opPattern","COPY",FACE,{"derivedFrom":subQ1,"instanceName":"78"}),makeQuery(id+"F3.opPattern","COPY",FACE,{"derivedFrom":subQ1,"instanceName":"79"}),makeQuery(id+"F3.opPattern","COPY",FACE,{"derivedFrom":subQ1,"instanceName":"80"}),makeQuery(id+"F3.opPattern","COPY",FACE,{"derivedFrom":subQ1,"instanceName":"81"}),makeQuery(id+"F3.opPattern","COPY",FACE,{"derivedFrom":subQ1,"instanceName":"82"}),makeQuery(id+"F3.opPattern","COPY",FACE,{"derivedFrom":subQ1,"instanceName":"83"}),makeQuery(id+"F3.opPattern","COPY",FACE,{"derivedFrom":subQ1,"instanceName":"84"}),makeQuery(id+"F3.opPattern","COPY",FACE,{"derivedFrom":subQ1,"instanceName":"85"}),makeQuery(id+"F3.opPattern","COPY",FACE,{"derivedFrom":subQ1,"instanceName":"86"}),makeQuery(id+"F3.opPattern","COPY",FACE,{"derivedFrom":subQ1,"instanceName":"87"}),makeQuery(id+"F3.opPattern","COPY",FACE,{"derivedFrom":subQ1,"instanceName":"88"}),makeQuery(id+"F3.opPattern","COPY",FACE,{"derivedFrom":subQ1,"instanceName":"89"}),makeQuery(id+"F3.opPattern","COPY",FACE,{"derivedFrom":subQ1,"instanceName":"90"}),makeQuery(id+"F3.opPattern","COPY",FACE,{"derivedFrom":subQ1,"instanceName":"91"}),makeQuery(id+"F3.opPattern","COPY",FACE,{"derivedFrom":subQ1,"instanceName":"92"}),makeQuery(id+"F3.opPattern","COPY",FACE,{"derivedFrom":subQ1,"instanceName":"93"}),makeQuery(id+"F3.opPattern","COPY",FACE,{"derivedFrom":subQ1,"instanceName":"94"}),makeQuery(id+"F3.opPattern","COPY",FACE,{"derivedFrom":subQ1,"instanceName":"95"}),makeQuery(id+"F3.opPattern","COPY",FACE,{"derivedFrom":subQ1,"instanceName":"96"}),makeQuery(id+"F3.opPattern","COPY",FACE,{"derivedFrom":subQ1,"instanceName":"97"}),makeQuery(id+"F3.opPattern","COPY",FACE,{"derivedFrom":subQ1,"instanceName":"98"}),makeQuery(id+"F3.opPattern","COPY",FACE,{"derivedFrom":subQ1,"instanceName":"99"}),makeQuery(id+"F3.opPattern","COPY",FACE,{"derivedFrom":subQ1,"instanceName":"100"}),makeQuery(id+"F3.opPattern","COPY",FACE,{"derivedFrom":subQ1,"instanceName":"101"}),makeQuery(id+"F3.opPattern","COPY",FACE,{"derivedFrom":subQ1,"instanceName":"102"}),makeQuery(id+"F3.opPattern","COPY",FACE,{"derivedFrom":subQ1,"instanceName":"103"}),makeQuery(id+"F3.opPattern","COPY",FACE,{"derivedFrom":subQ1,"instanceName":"104"}),makeQuery(id+"F3.opPattern","COPY",FACE,{"derivedFrom":subQ1,"instanceName":"105"}),makeQuery(id+"F3.opPattern","COPY",FACE,{"derivedFrom":subQ1,"instanceName":"106"}),makeQuery(id+"F3.opPattern","COPY",FACE,{"derivedFrom":subQ1,"instanceName":"107"}),makeQuery(id+"F3.opPattern","COPY",FACE,{"derivedFrom":subQ1,"instanceName":"108"}),makeQuery(id+"F3.opPattern","COPY",FACE,{"derivedFrom":subQ1,"instanceName":"109"}),makeQuery(id+"F3.opPattern","COPY",FACE,{"derivedFrom":subQ1,"instanceName":"110"}),makeQuery(id+"F3.opPattern","COPY",FACE,{"derivedFrom":subQ1,"instanceName":"111"}),makeQuery(id+"F3.opPattern","COPY",FACE,{"derivedFrom":subQ1,"instanceName":"112"}),makeQuery(id+"F3.opPattern","COPY",FACE,{"derivedFrom":subQ1,"instanceName":"113"}),makeQuery(id+"F3.opPattern","COPY",FACE,{"derivedFrom":subQ1,"instanceName":"114"}),makeQuery(id+"F3.opPattern","COPY",FACE,{"derivedFrom":subQ1,"instanceName":"115"}),makeQuery(id+"F3.opPattern","COPY",FACE,{"derivedFrom":subQ1,"instanceName":"116"}),makeQuery(id+"F3.opPattern","COPY",FACE,{"derivedFrom":subQ1,"instanceName":"117"}),makeQuery(id+"F3.opPattern","COPY",FACE,{"derivedFrom":subQ1,"instanceName":"118"}),makeQuery(id+"F3.opPattern","COPY",FACE,{"derivedFrom":subQ1,"instanceName":"119"}),makeQuery(id+"F3.opPattern","COPY",FACE,{"derivedFrom":subQ1,"instanceName":"120"}),makeQuery(id+"F3.opPattern","COPY",FACE,{"derivedFrom":subQ1,"instanceName":"121"}),makeQuery(id+"F3.opPattern","COPY",FACE,{"derivedFrom":subQ1,"instanceName":"122"}),makeQuery(id+"F3.opPattern","COPY",FACE,{"derivedFrom":subQ1,"instanceName":"123"}),makeQuery(id+"F3.opPattern","COPY",FACE,{"derivedFrom":subQ1,"instanceName":"124"}),makeQuery(id+"F3.opPattern","COPY",FACE,{"derivedFrom":subQ1,"instanceName":"125"}),makeQuery(id+"F3.opPattern","COPY",FACE,{"derivedFrom":subQ1,"instanceName":"126"}),makeQuery(id+"F3.opPattern","COPY",FACE,{"derivedFrom":subQ1,"instanceName":"127"}),makeQuery(id+"F3.opPattern","COPY",FACE,{"derivedFrom":subQ1,"instanceName":"128"}),makeQuery(id+"F3.opPattern","COPY",FACE,{"derivedFrom":subQ1,"instanceName":"129"}),makeQuery(id+"F3.opPattern","COPY",FACE,{"derivedFrom":subQ1,"instanceName":"130"}),makeQuery(id+"F3.opPattern","COPY",FACE,{"derivedFrom":subQ1,"instanceName":"131"})]});}
            var sketch = newSketch(context, id + "F11", { "sketchPlane" : qUnion([Q0])});
            skCircle(sketch, "E27.0", {"center": v(0, 0) * mm, "radius": 14.29 * mm});
            skCircle(sketch, "E27.1", {"center": v(23.81, 0) * mm, "radius": 2.41 * mm});
            skCircle(sketch, "E27.2", {"center": v(11.9, 20.62) * mm, "radius": 2.41 * mm});
            skCircle(sketch, "E27.5", {"center": v(-11.9, -20.62) * mm, "radius": 2.41 * mm});
            skCircle(sketch, "E28.0", {"center": v(-23.81, 0) * mm, "radius": 2.41 * mm});
            skCircle(sketch, "E28.1", {"center": v(11.9, -20.62) * mm, "radius": 2.41 * mm});
            skCircle(sketch, "E28.2", {"center": v(-11.9, 20.62) * mm, "radius": 2.41 * mm});
            skArc(sketch, "E29.0", {"start": v(27.6, -9.98) * mm, "mid": v(23.37, -13.5) * mm, "end": v(22.44, -18.9) * mm});
            skArc(sketch, "E29.1", {"start": v(29.08, -8.9) * mm, "mid": v(28.42, -9.55) * mm, "end": v(27.6, -9.98) * mm});
            skArc(sketch, "E29.2", {"start": v(22.44, -18.9) * mm, "mid": v(22.48, -19.84) * mm, "end": v(22.24, -20.74) * mm});
            skArc(sketch, "E29.3", {"start": v(6.84, -29.63) * mm, "mid": v(5.94, -29.38) * mm, "end": v(5.15, -28.89) * mm});
            skArc(sketch, "E29.4", {"start": v(5.15, -28.89) * mm, "mid": v(0, -26.99) * mm, "end": v(-5.15, -28.89) * mm});
            skArc(sketch, "E29.5", {"start": v(-5.15, -28.89) * mm, "mid": v(-5.94, -29.38) * mm, "end": v(-6.84, -29.63) * mm});
            skArc(sketch, "E29.6", {"start": v(27.6, 9.98) * mm, "mid": v(28.42, 9.55) * mm, "end": v(29.08, 8.9) * mm});
            skArc(sketch, "E29.7", {"start": v(22.44, 18.9) * mm, "mid": v(23.37, 13.5) * mm, "end": v(27.6, 9.98) * mm});
            skArc(sketch, "E29.8", {"start": v(22.24, 20.74) * mm, "mid": v(22.48, 19.84) * mm, "end": v(22.44, 18.9) * mm});
            skArc(sketch, "E29.9", {"start": v(5.15, 28.89) * mm, "mid": v(5.94, 29.38) * mm, "end": v(6.84, 29.63) * mm});
            skArc(sketch, "E29.10", {"start": v(-5.15, 28.89) * mm, "mid": v(0, 26.99) * mm, "end": v(5.15, 28.89) * mm});
            skArc(sketch, "E29.11", {"start": v(-6.84, 29.63) * mm, "mid": v(-5.94, 29.38) * mm, "end": v(-5.15, 28.89) * mm});
            skArc(sketch, "E29.12", {"start": v(-22.44, 18.9) * mm, "mid": v(-22.48, 19.84) * mm, "end": v(-22.24, 20.74) * mm});
            skArc(sketch, "E29.13", {"start": v(-27.6, 9.98) * mm, "mid": v(-23.37, 13.5) * mm, "end": v(-22.44, 18.9) * mm});
            skArc(sketch, "E29.14", {"start": v(-29.08, 8.9) * mm, "mid": v(-28.42, 9.55) * mm, "end": v(-27.6, 9.98) * mm});
            skArc(sketch, "E29.15", {"start": v(-27.6, -9.98) * mm, "mid": v(-28.42, -9.55) * mm, "end": v(-29.08, -8.9) * mm});
            skArc(sketch, "E29.16", {"start": v(-22.44, -18.9) * mm, "mid": v(-23.37, -13.5) * mm, "end": v(-27.6, -9.98) * mm});
            skArc(sketch, "E29.17", {"start": v(-22.24, -20.74) * mm, "mid": v(-22.48, -19.84) * mm, "end": v(-22.44, -18.9) * mm});
            skArc(sketch, "E30", {"start": v(29.08, -8.9) * mm, "mid": v(30.4, 0) * mm, "end": v(29.08, 8.9) * mm});
            skArc(sketch, "E31.trimOffspring", {"start": v(22.24, 20.74) * mm, "mid": v(15.2, 26.33) * mm, "end": v(6.84, 29.63) * mm});
            skArc(sketch, "E32.trimOffspring", {"start": v(-6.84, 29.63) * mm, "mid": v(-15.2, 26.33) * mm, "end": v(-22.24, 20.74) * mm});
            skArc(sketch, "E33.trimOffspring", {"start": v(-29.08, 8.9) * mm, "mid": v(-30.4, 0) * mm, "end": v(-29.08, -8.9) * mm});
            skArc(sketch, "E34.trimOffspring", {"start": v(-22.24, -20.74) * mm, "mid": v(-15.2, -26.33) * mm, "end": v(-6.84, -29.63) * mm});
            skArc(sketch, "E35.trimOffspring", {"start": v(6.84, -29.63) * mm, "mid": v(15.2, -26.33) * mm, "end": v(22.24, -20.74) * mm});
            skSolve(sketch);
        }
        {
            var Q0;
            Q0=qSketchRegion(id+"F11",true);
            extrude(context, id + "F12", {"entities" : qUnion([Q0]), "depth" : 3.17 * mm});
        }
        {
            var Q0;
            {var subQ0=sQuery(id+"F0.wireOp",EDGE,"E7");var subQ1=makeQuery(id+"F2.opExtrude","CAP_FACE",FACE,{"disambiguationData":[OSD([sQuery(id+"F0.wireOp",EDGE,"E2"),sQuery(id+"F0.wireOp",EDGE,"E3"),sQuery(id+"F0.wireOp",EDGE,"E4"),sQuery(id+"F0.wireOp",EDGE,"E5"),sQuery(id+"F0.wireOp",EDGE,"E6"),subQ0])],"isStart":true});Q0=makeQuery(id+"F3.boolean.opBoolean","MERGE",FACE,{"derivedFrom":[makeQuery(id+"F1.opExtrude","CAP_FACE",FACE,{"disambiguationData":[OSD([sQuery(id+"F0.wireOp",EDGE,"E0"),sQuery(id+"F0.wireOp",EDGE,"E1"),subQ0])],"isStart":true}),subQ1,makeQuery(id+"F3.opPattern","COPY",FACE,{"derivedFrom":subQ1,"instanceName":"1"}),makeQuery(id+"F3.opPattern","COPY",FACE,{"derivedFrom":subQ1,"instanceName":"2"}),makeQuery(id+"F3.opPattern","COPY",FACE,{"derivedFrom":subQ1,"instanceName":"3"}),makeQuery(id+"F3.opPattern","COPY",FACE,{"derivedFrom":subQ1,"instanceName":"4"}),makeQuery(id+"F3.opPattern","COPY",FACE,{"derivedFrom":subQ1,"instanceName":"5"}),makeQuery(id+"F3.opPattern","COPY",FACE,{"derivedFrom":subQ1,"instanceName":"6"}),makeQuery(id+"F3.opPattern","COPY",FACE,{"derivedFrom":subQ1,"instanceName":"7"}),makeQuery(id+"F3.opPattern","COPY",FACE,{"derivedFrom":subQ1,"instanceName":"8"}),makeQuery(id+"F3.opPattern","COPY",FACE,{"derivedFrom":subQ1,"instanceName":"9"}),makeQuery(id+"F3.opPattern","COPY",FACE,{"derivedFrom":subQ1,"instanceName":"10"}),makeQuery(id+"F3.opPattern","COPY",FACE,{"derivedFrom":subQ1,"instanceName":"11"}),makeQuery(id+"F3.opPattern","COPY",FACE,{"derivedFrom":subQ1,"instanceName":"12"}),makeQuery(id+"F3.opPattern","COPY",FACE,{"derivedFrom":subQ1,"instanceName":"13"}),makeQuery(id+"F3.opPattern","COPY",FACE,{"derivedFrom":subQ1,"instanceName":"14"}),makeQuery(id+"F3.opPattern","COPY",FACE,{"derivedFrom":subQ1,"instanceName":"15"}),makeQuery(id+"F3.opPattern","COPY",FACE,{"derivedFrom":subQ1,"instanceName":"16"}),makeQuery(id+"F3.opPattern","COPY",FACE,{"derivedFrom":subQ1,"instanceName":"17"}),makeQuery(id+"F3.opPattern","COPY",FACE,{"derivedFrom":subQ1,"instanceName":"18"}),makeQuery(id+"F3.opPattern","COPY",FACE,{"derivedFrom":subQ1,"instanceName":"19"}),makeQuery(id+"F3.opPattern","COPY",FACE,{"derivedFrom":subQ1,"instanceName":"20"}),makeQuery(id+"F3.opPattern","COPY",FACE,{"derivedFrom":subQ1,"instanceName":"21"}),makeQuery(id+"F3.opPattern","COPY",FACE,{"derivedFrom":subQ1,"instanceName":"22"}),makeQuery(id+"F3.opPattern","COPY",FACE,{"derivedFrom":subQ1,"instanceName":"23"}),makeQuery(id+"F3.opPattern","COPY",FACE,{"derivedFrom":subQ1,"instanceName":"24"}),makeQuery(id+"F3.opPattern","COPY",FACE,{"derivedFrom":subQ1,"instanceName":"25"}),makeQuery(id+"F3.opPattern","COPY",FACE,{"derivedFrom":subQ1,"instanceName":"26"}),makeQuery(id+"F3.opPattern","COPY",FACE,{"derivedFrom":subQ1,"instanceName":"27"}),makeQuery(id+"F3.opPattern","COPY",FACE,{"derivedFrom":subQ1,"instanceName":"28"}),makeQuery(id+"F3.opPattern","COPY",FACE,{"derivedFrom":subQ1,"instanceName":"29"}),makeQuery(id+"F3.opPattern","COPY",FACE,{"derivedFrom":subQ1,"instanceName":"30"}),makeQuery(id+"F3.opPattern","COPY",FACE,{"derivedFrom":subQ1,"instanceName":"31"}),makeQuery(id+"F3.opPattern","COPY",FACE,{"derivedFrom":subQ1,"instanceName":"32"}),makeQuery(id+"F3.opPattern","COPY",FACE,{"derivedFrom":subQ1,"instanceName":"33"}),makeQuery(id+"F3.opPattern","COPY",FACE,{"derivedFrom":subQ1,"instanceName":"34"}),makeQuery(id+"F3.opPattern","COPY",FACE,{"derivedFrom":subQ1,"instanceName":"35"}),makeQuery(id+"F3.opPattern","COPY",FACE,{"derivedFrom":subQ1,"instanceName":"36"}),makeQuery(id+"F3.opPattern","COPY",FACE,{"derivedFrom":subQ1,"instanceName":"37"}),makeQuery(id+"F3.opPattern","COPY",FACE,{"derivedFrom":subQ1,"instanceName":"38"}),makeQuery(id+"F3.opPattern","COPY",FACE,{"derivedFrom":subQ1,"instanceName":"39"}),makeQuery(id+"F3.opPattern","COPY",FACE,{"derivedFrom":subQ1,"instanceName":"40"}),makeQuery(id+"F3.opPattern","COPY",FACE,{"derivedFrom":subQ1,"instanceName":"41"}),makeQuery(id+"F3.opPattern","COPY",FACE,{"derivedFrom":subQ1,"instanceName":"42"}),makeQuery(id+"F3.opPattern","COPY",FACE,{"derivedFrom":subQ1,"instanceName":"43"}),makeQuery(id+"F3.opPattern","COPY",FACE,{"derivedFrom":subQ1,"instanceName":"44"}),makeQuery(id+"F3.opPattern","COPY",FACE,{"derivedFrom":subQ1,"instanceName":"45"}),makeQuery(id+"F3.opPattern","COPY",FACE,{"derivedFrom":subQ1,"instanceName":"46"}),makeQuery(id+"F3.opPattern","COPY",FACE,{"derivedFrom":subQ1,"instanceName":"47"}),makeQuery(id+"F3.opPattern","COPY",FACE,{"derivedFrom":subQ1,"instanceName":"48"}),makeQuery(id+"F3.opPattern","COPY",FACE,{"derivedFrom":subQ1,"instanceName":"49"}),makeQuery(id+"F3.opPattern","COPY",FACE,{"derivedFrom":subQ1,"instanceName":"50"}),makeQuery(id+"F3.opPattern","COPY",FACE,{"derivedFrom":subQ1,"instanceName":"51"}),makeQuery(id+"F3.opPattern","COPY",FACE,{"derivedFrom":subQ1,"instanceName":"52"}),makeQuery(id+"F3.opPattern","COPY",FACE,{"derivedFrom":subQ1,"instanceName":"53"}),makeQuery(id+"F3.opPattern","COPY",FACE,{"derivedFrom":subQ1,"instanceName":"54"}),makeQuery(id+"F3.opPattern","COPY",FACE,{"derivedFrom":subQ1,"instanceName":"55"}),makeQuery(id+"F3.opPattern","COPY",FACE,{"derivedFrom":subQ1,"instanceName":"56"}),makeQuery(id+"F3.opPattern","COPY",FACE,{"derivedFrom":subQ1,"instanceName":"57"}),makeQuery(id+"F3.opPattern","COPY",FACE,{"derivedFrom":subQ1,"instanceName":"58"}),makeQuery(id+"F3.opPattern","COPY",FACE,{"derivedFrom":subQ1,"instanceName":"59"}),makeQuery(id+"F3.opPattern","COPY",FACE,{"derivedFrom":subQ1,"instanceName":"60"}),makeQuery(id+"F3.opPattern","COPY",FACE,{"derivedFrom":subQ1,"instanceName":"61"}),makeQuery(id+"F3.opPattern","COPY",FACE,{"derivedFrom":subQ1,"instanceName":"62"}),makeQuery(id+"F3.opPattern","COPY",FACE,{"derivedFrom":subQ1,"instanceName":"63"}),makeQuery(id+"F3.opPattern","COPY",FACE,{"derivedFrom":subQ1,"instanceName":"64"}),makeQuery(id+"F3.opPattern","COPY",FACE,{"derivedFrom":subQ1,"instanceName":"65"}),makeQuery(id+"F3.opPattern","COPY",FACE,{"derivedFrom":subQ1,"instanceName":"66"}),makeQuery(id+"F3.opPattern","COPY",FACE,{"derivedFrom":subQ1,"instanceName":"67"}),makeQuery(id+"F3.opPattern","COPY",FACE,{"derivedFrom":subQ1,"instanceName":"68"}),makeQuery(id+"F3.opPattern","COPY",FACE,{"derivedFrom":subQ1,"instanceName":"69"}),makeQuery(id+"F3.opPattern","COPY",FACE,{"derivedFrom":subQ1,"instanceName":"70"}),makeQuery(id+"F3.opPattern","COPY",FACE,{"derivedFrom":subQ1,"instanceName":"71"}),makeQuery(id+"F3.opPattern","COPY",FACE,{"derivedFrom":subQ1,"instanceName":"72"}),makeQuery(id+"F3.opPattern","COPY",FACE,{"derivedFrom":subQ1,"instanceName":"73"}),makeQuery(id+"F3.opPattern","COPY",FACE,{"derivedFrom":subQ1,"instanceName":"74"}),makeQuery(id+"F3.opPattern","COPY",FACE,{"derivedFrom":subQ1,"instanceName":"75"}),makeQuery(id+"F3.opPattern","COPY",FACE,{"derivedFrom":subQ1,"instanceName":"76"}),makeQuery(id+"F3.opPattern","COPY",FACE,{"derivedFrom":subQ1,"instanceName":"77"}),makeQuery(id+"F3.opPattern","COPY",FACE,{"derivedFrom":subQ1,"instanceName":"78"}),makeQuery(id+"F3.opPattern","COPY",FACE,{"derivedFrom":subQ1,"instanceName":"79"}),makeQuery(id+"F3.opPattern","COPY",FACE,{"derivedFrom":subQ1,"instanceName":"80"}),makeQuery(id+"F3.opPattern","COPY",FACE,{"derivedFrom":subQ1,"instanceName":"81"}),makeQuery(id+"F3.opPattern","COPY",FACE,{"derivedFrom":subQ1,"instanceName":"82"}),makeQuery(id+"F3.opPattern","COPY",FACE,{"derivedFrom":subQ1,"instanceName":"83"}),makeQuery(id+"F3.opPattern","COPY",FACE,{"derivedFrom":subQ1,"instanceName":"84"}),makeQuery(id+"F3.opPattern","COPY",FACE,{"derivedFrom":subQ1,"instanceName":"85"}),makeQuery(id+"F3.opPattern","COPY",FACE,{"derivedFrom":subQ1,"instanceName":"86"}),makeQuery(id+"F3.opPattern","COPY",FACE,{"derivedFrom":subQ1,"instanceName":"87"}),makeQuery(id+"F3.opPattern","COPY",FACE,{"derivedFrom":subQ1,"instanceName":"88"}),makeQuery(id+"F3.opPattern","COPY",FACE,{"derivedFrom":subQ1,"instanceName":"89"}),makeQuery(id+"F3.opPattern","COPY",FACE,{"derivedFrom":subQ1,"instanceName":"90"}),makeQuery(id+"F3.opPattern","COPY",FACE,{"derivedFrom":subQ1,"instanceName":"91"}),makeQuery(id+"F3.opPattern","COPY",FACE,{"derivedFrom":subQ1,"instanceName":"92"}),makeQuery(id+"F3.opPattern","COPY",FACE,{"derivedFrom":subQ1,"instanceName":"93"}),makeQuery(id+"F3.opPattern","COPY",FACE,{"derivedFrom":subQ1,"instanceName":"94"}),makeQuery(id+"F3.opPattern","COPY",FACE,{"derivedFrom":subQ1,"instanceName":"95"}),makeQuery(id+"F3.opPattern","COPY",FACE,{"derivedFrom":subQ1,"instanceName":"96"}),makeQuery(id+"F3.opPattern","COPY",FACE,{"derivedFrom":subQ1,"instanceName":"97"}),makeQuery(id+"F3.opPattern","COPY",FACE,{"derivedFrom":subQ1,"instanceName":"98"}),makeQuery(id+"F3.opPattern","COPY",FACE,{"derivedFrom":subQ1,"instanceName":"99"}),makeQuery(id+"F3.opPattern","COPY",FACE,{"derivedFrom":subQ1,"instanceName":"100"}),makeQuery(id+"F3.opPattern","COPY",FACE,{"derivedFrom":subQ1,"instanceName":"101"}),makeQuery(id+"F3.opPattern","COPY",FACE,{"derivedFrom":subQ1,"instanceName":"102"}),makeQuery(id+"F3.opPattern","COPY",FACE,{"derivedFrom":subQ1,"instanceName":"103"}),makeQuery(id+"F3.opPattern","COPY",FACE,{"derivedFrom":subQ1,"instanceName":"104"}),makeQuery(id+"F3.opPattern","COPY",FACE,{"derivedFrom":subQ1,"instanceName":"105"}),makeQuery(id+"F3.opPattern","COPY",FACE,{"derivedFrom":subQ1,"instanceName":"106"}),makeQuery(id+"F3.opPattern","COPY",FACE,{"derivedFrom":subQ1,"instanceName":"107"}),makeQuery(id+"F3.opPattern","COPY",FACE,{"derivedFrom":subQ1,"instanceName":"108"}),makeQuery(id+"F3.opPattern","COPY",FACE,{"derivedFrom":subQ1,"instanceName":"109"}),makeQuery(id+"F3.opPattern","COPY",FACE,{"derivedFrom":subQ1,"instanceName":"110"}),makeQuery(id+"F3.opPattern","COPY",FACE,{"derivedFrom":subQ1,"instanceName":"111"}),makeQuery(id+"F3.opPattern","COPY",FACE,{"derivedFrom":subQ1,"instanceName":"112"}),makeQuery(id+"F3.opPattern","COPY",FACE,{"derivedFrom":subQ1,"instanceName":"113"}),makeQuery(id+"F3.opPattern","COPY",FACE,{"derivedFrom":subQ1,"instanceName":"114"}),makeQuery(id+"F3.opPattern","COPY",FACE,{"derivedFrom":subQ1,"instanceName":"115"}),makeQuery(id+"F3.opPattern","COPY",FACE,{"derivedFrom":subQ1,"instanceName":"116"}),makeQuery(id+"F3.opPattern","COPY",FACE,{"derivedFrom":subQ1,"instanceName":"117"}),makeQuery(id+"F3.opPattern","COPY",FACE,{"derivedFrom":subQ1,"instanceName":"118"}),makeQuery(id+"F3.opPattern","COPY",FACE,{"derivedFrom":subQ1,"instanceName":"119"}),makeQuery(id+"F3.opPattern","COPY",FACE,{"derivedFrom":subQ1,"instanceName":"120"}),makeQuery(id+"F3.opPattern","COPY",FACE,{"derivedFrom":subQ1,"instanceName":"121"}),makeQuery(id+"F3.opPattern","COPY",FACE,{"derivedFrom":subQ1,"instanceName":"122"}),makeQuery(id+"F3.opPattern","COPY",FACE,{"derivedFrom":subQ1,"instanceName":"123"}),makeQuery(id+"F3.opPattern","COPY",FACE,{"derivedFrom":subQ1,"instanceName":"124"}),makeQuery(id+"F3.opPattern","COPY",FACE,{"derivedFrom":subQ1,"instanceName":"125"}),makeQuery(id+"F3.opPattern","COPY",FACE,{"derivedFrom":subQ1,"instanceName":"126"}),makeQuery(id+"F3.opPattern","COPY",FACE,{"derivedFrom":subQ1,"instanceName":"127"}),makeQuery(id+"F3.opPattern","COPY",FACE,{"derivedFrom":subQ1,"instanceName":"128"}),makeQuery(id+"F3.opPattern","COPY",FACE,{"derivedFrom":subQ1,"instanceName":"129"}),makeQuery(id+"F3.opPattern","COPY",FACE,{"derivedFrom":subQ1,"instanceName":"130"}),makeQuery(id+"F3.opPattern","COPY",FACE,{"derivedFrom":subQ1,"instanceName":"131"})]});}
            var sketch = newSketch(context, id + "F13", { "sketchPlane" : qUnion([Q0])});
            skCircle(sketch, "E36.0", {"center": v(-23.81, 0) * mm, "radius": 2.41 * mm});
            skCircle(sketch, "E36.1", {"center": v(-11.9, 20.62) * mm, "radius": 2.41 * mm});
            skCircle(sketch, "E36.2", {"center": v(11.9, 20.62) * mm, "radius": 2.41 * mm});
            skCircle(sketch, "E36.3", {"center": v(23.81, 0) * mm, "radius": 2.41 * mm});
            skCircle(sketch, "E36.4", {"center": v(11.9, -20.62) * mm, "radius": 2.41 * mm});
            skCircle(sketch, "E36.5", {"center": v(-11.9, -20.62) * mm, "radius": 2.41 * mm});
            skSolve(sketch);
        }
        {
            var Q0;
            Q0=sQuery(id+"F13.wireOp",VERTEX,"E36.4.center");
            var Q1;
            Q1=sQuery(id+"F13.wireOp",VERTEX,"E36.3.center");
            var Q2;
            Q2=sQuery(id+"F13.wireOp",VERTEX,"E36.2.center");
            var Q3;
            Q3=sQuery(id+"F13.wireOp",VERTEX,"E36.1.center");
            var Q4;
            Q4=sQuery(id+"F13.wireOp",VERTEX,"E36.0.center");
            var Q5;
            Q5=sQuery(id+"F13.wireOp",VERTEX,"E36.5.center");
            var Q6;
            Q6=makeQuery(id+"F1.opExtrude","SWEPT_BODY",BODY,{"disambiguationData":[OSD([sQuery(id+"F0.wireOp",EDGE,"E0"),sQuery(id+"F0.wireOp",EDGE,"E1"),sQuery(id+"F0.wireOp",EDGE,"E7")])]});
            hole(context, id + "F14", {"style" : HoleStyle.C_BORE, "holeDiameter" : 4.83 * mm, "cBoreDiameter" : 7.94 * mm, "cBoreDepth" : 4.83 * mm, "endStyle" : HoleEndStyle.THROUGH, "locations" : qUnion([Q0, Q1, Q2, Q3, Q4, Q5]), "scope" : qUnion([Q6])});
        }
    });
